FCSTD DOCUMENT  (FreeCAD 0.20R29410 (Git))
Label: wearableV5Plus_m3_May_1_m3_2023
License: All rights reserved
LicenseURL: http://en.wikipedia.org/wiki/All_rights_reserved
objects: Part::Feature×57, Sketcher::SketchObject×23, Part::Extrusion×23, Part::MultiFuse×12, Part::Fillet×10, Part::Cut×10, Part::Box×9, App::Part×9, Part::Cylinder×4, Mesh::Feature×2, Part::Compound×1
note: 149 computed .brp shape members not serialized (recipe doc carries the construction recipe); baked Part::Feature solids carry a one-line shape summary decoded from their .brp

FEATURE [Part::Box] Box  label="batteryPlus"
  AttacherType = Attacher::AttachEngine3D
  Height = 11
  Length = 68
  Placement = pos=(3,3,2) rot=(0,0,1;0rad)
  Width = 56
FEATURE [Mesh::Feature] pisugar3Board
  Placement = pos=(-2.89,36.08,0.25) rot=(-1,0,0;4.71239rad)
FEATURE [Part::Feature] Part__Feature001  label="RaspberryPiZeroW"
  Placement = pos=(36.5,18,19.18) rot=(1,0,0;1.5708rad)
  shape: bbox 65.9 x 31.25 x 4.8 mm, 368 faces, 2 solids (baked)
FEATURE [Part::Feature] Part__Feature  label="ips7100"
  Placement = pos=(-24,0,222) rot=(0.999993,-0.003655,0;3.14159rad)
  shape: bbox 48.14 x 14.05 x 44.14 mm, 1935 faces (baked)
FEATURE [Part::Compound] Compound  label="ips7100s"
  Links = -> [Part__Feature]
  Placement = pos=(13.15,34,29) rot=(0,0.707107,0.707107;3.15032rad)
FEATURE [Part::Feature] Part__Feature002  label="Printed Circuit Board"
  shape: bbox 25.4 x 17.78 x 1.6 mm, 42 faces (baked)
FEATURE [Part::Feature] Part__Feature003  label="EAHC2835WD6"
  shape: bbox 3.513 x 2.813 x 0.7485 mm, 108 faces, 4 solids (baked)
FEATURE [Part::Feature] Part__Feature004  label="AS7341 v2"
  Placement = pos=(0,-0.339822,1.6) rot=(0,0,1;0rad)
  shape: bbox 2 x 3.1 x 1.1 mm, 267 faces, 26 solids (baked)
FEATURE [Part::Feature] Part__Feature005  label="CAPC-0805-T0.95-BN v1"
  Placement = pos=(-5.01759,-3.15294,1.6) rot=(0,0,1;0rad)
  shape: bbox 2.1 x 1.35 x 0.95 mm, 42 faces (baked)
FEATURE [Part::Feature] Part__Feature006  label="CAPC-0805-T0.95-BN v002"
  Placement = pos=(-5.48627,2.66154,1.6) rot=(0,0,-1;1.5708rad)
  shape: bbox 1.35 x 2.1 x 0.95 mm, 42 faces (baked)
FEATURE [Part::Feature] Part__Feature007  label="CAPC-0805-T0.95-BN v003"
  Placement = pos=(-3.43627,2.66154,1.6) rot=(0,0,-1;1.5708rad)
  shape: bbox 1.35 x 2.1 x 0.95 mm, 42 faces (baked)
FEATURE [Part::Feature] Part__Feature008  label="CAPC-0603-T0.9-BN v1"
  Placement = pos=(-1.69987,-3.28475,1.6) rot=(0,0,1;0rad)
  shape: bbox 1.7 x 0.9 x 0.9 mm, 42 faces (baked)
FEATURE [Part::Feature] Part__Feature009  label="BODY_MF06A"
  Placement = pos=(0,0,0.762) rot=(0.57735,-0.57735,-0.57735;2.0944rad)
  shape: bbox 1.601 x 2.921 x 1.016 mm, 42 faces (baked)
FEATURE [Part::Feature] Part__Feature010  label="LEAD_MF06A"
  Placement = pos=(-0.9652,-0.9525,0.1016) rot=(0.57735,-0.57735,-0.57735;2.0944rad)
  shape: bbox 0.6223 x 0.3749 x 0.8636 mm, 14 faces (baked)
FEATURE [Part::Feature] Part__Feature011  label="LEAD_MF06A001"
  Placement = pos=(-0.9652,0,0.1016) rot=(0.57735,-0.57735,-0.57735;2.0944rad)
  shape: bbox 0.6223 x 0.3749 x 0.8636 mm, 14 faces (baked)
FEATURE [Part::Feature] Part__Feature012  label="LEAD_MF06A002"
  Placement = pos=(-0.9652,0.9525,0.1016) rot=(0.57735,-0.57735,-0.57735;2.0944rad)
  shape: bbox 0.6223 x 0.3749 x 0.8636 mm, 14 faces (baked)
FEATURE [Part::Feature] Part__Feature013  label="LEAD_MF06A003"
  Placement = pos=(0.9652,-0.9525,0.1016) rot=(0.57735,0.57735,0.57735;2.0944rad)
  shape: bbox 0.6223 x 0.3749 x 0.8636 mm, 14 faces (baked)
FEATURE [Part::Feature] Part__Feature014  label="LEAD_MF06A004"
  Placement = pos=(0.9652,0,0.1016) rot=(0.57735,0.57735,0.57735;2.0944rad)
  shape: bbox 0.6223 x 0.3749 x 0.8636 mm, 14 faces (baked)
FEATURE [Part::Feature] Part__Feature015  label="LEAD_MF06A005"
  Placement = pos=(0.9652,0.9525,0.1016) rot=(0.57735,0.57735,0.57735;2.0944rad)
  shape: bbox 0.6223 x 0.3749 x 0.8636 mm, 14 faces (baked)
FEATURE [Part::Feature] Part__Feature016  label="SOT363 v2"
  Placement = pos=(4.97054,-0.645171,1.675) rot=(0,0,1;3.14159rad)
  shape: bbox 2.1 x 2 x 1.1 mm, 94 faces, 7 solids (baked)
FEATURE [Part::Feature] Part__Feature017  label="LED 0603 single color v1"
  Placement = pos=(-9.18406,3.72778,1.60762) rot=(0,0,1;1.5708rad)
  shape: bbox 1.961 x 0.7932 x 0.7145 mm, 63 faces, 5 solids (baked)
FEATURE [Part::Feature] Part__Feature018  label="RESC-0603 v1"
  Placement = pos=(4.83432,-3.67461,1.6) rot=(0,0,1;0rad)
  shape: bbox 1.7 x 0.9 x 0.55 mm, 52 faces, 3 solids (baked)
FEATURE [Part::Feature] Part__Feature019  label="RESC-0603 v002"
  Placement = pos=(-7.14949,3.61248,1.6) rot=(0,0,-1;1.5708rad)
  shape: bbox 0.9 x 1.7 x 0.55 mm, 52 faces, 3 solids (baked)
FEATURE [Part::Feature] Part__Feature020  label="YC164_RESPACK v1"
  Placement = pos=(2.99591,1.52916,1.6) rot=(0,0,1;0rad)
  shape: bbox 3.2 x 1.6 x 0.61 mm, 172 faces (baked)
FEATURE [Part::Feature] Part__Feature021  label="qwicc v2"
  Placement = pos=(-10.8364,0.0607456,1.65) rot=(0,0,-1;1.5708rad)
  shape: bbox 4.95 x 6 x 2.96 mm, 229 faces, 7 solids (baked)
FEATURE [Part::Feature] Part__Feature022  label="qwicc v003"
  Placement = pos=(10.8256,0.00556102,1.65) rot=(0,0,1;1.5708rad)
  shape: bbox 4.95 x 6 x 2.96 mm, 229 faces, 7 solids (baked)
FEATURE [Part::Feature] Part__Feature023  label="scd30"
  Placement = pos=(20,68.5,5.75) rot=(1,0,0;1.5708rad)
  shape: bbox 35.11 x 23.02 x 7.027 mm, 2292 faces, 25 solids (baked)
FEATURE [App::Part] sot_23_6_v2  label="sot-23-6 v2"
  Group = -> [Part__Feature009,Part__Feature010,Part__Feature011,Part__Feature012,Part__Feature013,Part__Feature014,Part__Feature015]
  Origin = -> Origin
  Placement = pos=(-4.47945,-0.603742,1.69152) rot=(0,0,1;0rad)
FEATURE [App::Part] Adafruit_AS7341_STEMMA_QT_v2  label="bme280"
  Group = -> [Part__Feature002,Part__Feature003,Part__Feature004,Part__Feature005,Part__Feature006,Part__Feature007,Part__Feature008,sot_23_6_v2,Part__Feature016,Part__Feature017,Part__Feature018,Part__Feature019,Part__Feature020,Part__Feature021,Part__Feature022]
  Origin = -> Origin001
  Placement = pos=(53,69,12) rot=(0,1,0;3.14159rad)
FEATURE [Part::Box] Box002  label="bottom"
  AttacherType = Attacher::AttachEngine3D
  Height = 27
  Length = 74
  Width = 91
FEATURE [Part::Fillet] Fillet  label="bottom002"
  Base = -> Box002
  Edges = 8 edges r=2: [Edge1,Edge3,Edge4,Edge5,Edge7,Edge8,Edge9,Edge11]
FEATURE [Part::Box] Box003  label="bottom001"
  AttacherType = Attacher::AttachEngine3D
  Height = 39
  Length = 70
  Placement = pos=(2,2,2) rot=(0,0,1;0rad)
  Width = 87
FEATURE [Part::Fillet] Fillet001  label="bottomCut"
  Base = -> Box003
  Edges = 8 edges r=2: [Edge1,Edge3,Edge4,Edge5,Edge7,Edge8,Edge9,Edge11]
FEATURE [Part::Cut] Cut  label="bottom003"
  Base = -> Fillet
  Tool = -> Fillet001
FEATURE [Part::Feature] Part__Feature024  label="Board"
  shape: bbox 25.4 x 25.4 x 1.57 mm, 211 faces (baked)
FEATURE [Part::Feature] Part__Feature025  label="QFN24_4MM"
  Placement = pos=(12.1412,14.4526,1.57) rot=(0,0,1;3.92699rad)
  shape: bbox 5.657 x 5.657 x 0.9 mm, 172 faces (baked)
FEATURE [Part::Feature] Part__Feature026  label="Part 5"
  shape: bbox 0.48 x 0.6603 x 0.6 mm, 14 faces (baked)
FEATURE [Part::Feature] Part__Feature027  label="Part 6"
  shape: bbox 0.48 x 0.6603 x 0.6 mm, 14 faces (baked)
FEATURE [Part::Feature] Part__Feature028  label="Part 4"
  shape: bbox 0.48 x 0.6603 x 0.6 mm, 14 faces (baked)
FEATURE [Part::Feature] Part__Feature029  label="Part 3"
  shape: bbox 0.48 x 0.6603 x 0.6 mm, 14 faces (baked)
FEATURE [Part::Feature] Part__Feature030  label="Part 2"
  shape: bbox 0.48 x 0.6603 x 0.6 mm, 14 faces (baked)
FEATURE [Part::Feature] Part__Feature031  label="Part 1"
  shape: bbox 3 x 1.4 x 1 mm, 10 faces (baked)
FEATURE [App::Part] _6700497  label="36700497"
  Group = -> [Part__Feature026,Part__Feature027,Part__Feature028,Part__Feature029,Part__Feature030,Part__Feature031]
  Origin = -> Origin002
  Placement = pos=(0,0,0) rot=(0,0,1;3.14159rad)
FEATURE [App::Part] SOT23_5  label="SOT23-5"
  Group = -> [_6700497]
  Origin = -> Origin003
  Placement = pos=(2.54,6.985,1.57) rot=(0,0,1;3.14159rad)
FEATURE [Part::Feature] Part__Feature032  label="Pin1"
  shape: bbox 0.6224 x 1.252 x 1.252 mm, 37 faces (baked)
FEATURE [Part::Feature] Part__Feature033  label="Pin2"
  shape: bbox 0.6224 x 1.252 x 1.252 mm, 37 faces (baked)
FEATURE [Part::Feature] Part__Feature034  label="CeramicBody"
  shape: bbox 1.8 x 1.23 x 1.23 mm, 10 faces (baked)
FEATURE [App::Part] _603_NO  label="0603-NO"
  Group = -> [Part__Feature032,Part__Feature033,Part__Feature034]
  Origin = -> Origin004
  Placement = pos=(16.51,8.382,1.57) rot=(0,0,1;0rad)
FEATURE [Part::Feature] Part__Feature035  label="0603-NO (1)"
  Placement = pos=(23.241,6.223,1.57) rot=(0,0,1;0rad)
  shape: bbox 1.7 x 0.9 x 0.55 mm, 52 faces, 3 solids (baked)
FEATURE [Part::Feature] Part__Feature036  label="0603-NO (2)"
  Placement = pos=(13.3858,8.4328,1.57) rot=(0,0,1;0rad)
  shape: bbox 1.7 x 0.9 x 0.55 mm, 52 faces, 3 solids (baked)
FEATURE [Part::Feature] Part__Feature037  label="0603-NO (3)"
  Placement = pos=(1.905,18.923,1.57) rot=(0,0,1;3.14159rad)
  shape: bbox 1.7 x 0.9 x 0.55 mm, 52 faces, 3 solids (baked)
FEATURE [Part::Feature] Part__Feature038  label="Pin1 (1)"
  shape: bbox 0.6224 x 1.252 x 1.252 mm, 37 faces (baked)
FEATURE [Part::Feature] Part__Feature039  label="Pin2 (1)"
  shape: bbox 0.6224 x 1.252 x 1.252 mm, 37 faces (baked)
FEATURE [Part::Feature] Part__Feature040  label="CeramicBody (1)"
  shape: bbox 1.8 x 1.23 x 1.23 mm, 10 faces (baked)
FEATURE [App::Part] _805_NO  label="0805-NO"
  Group = -> [Part__Feature038,Part__Feature039,Part__Feature040]
  Origin = -> Origin005
  Placement = pos=(7.874,13.589,1.57) rot=(0,0,1;1.5708rad)
FEATURE [Part::Feature] Part__Feature041  label="Pin1 (2)"
  shape: bbox 0.6224 x 1.252 x 1.252 mm, 37 faces (baked)
FEATURE [Part::Feature] Part__Feature042  label="Pin2 (2)"
  shape: bbox 0.6224 x 1.252 x 1.252 mm, 37 faces (baked)
FEATURE [Part::Feature] Part__Feature043  label="CeramicBody (2)"
  shape: bbox 1.8 x 1.23 x 1.23 mm, 10 faces (baked)
FEATURE [App::Part] _805_NO__1_  label="0805-NO (1)"
  Group = -> [Part__Feature041,Part__Feature042,Part__Feature043]
  Origin = -> Origin006
  Placement = pos=(12.827,6.223,1.57) rot=(0,0,1;3.14159rad)
FEATURE [Part::Feature] Part__Feature044  label="CHIPLED_0603_NOOUTLINE"
  Placement = pos=(23.368,8.509,1.57) rot=(0,0,1;1.5708rad)
  shape: bbox 1.616 x 0.8 x 0.4 mm, 133 faces (baked)
FEATURE [Part::Feature] Part__Feature045  label="CHIPLED_0603_NOOUTLINE (1)"
  Placement = pos=(1.905,16.764,1.57) rot=(0,0,-1;1.5708rad)
  shape: bbox 1.616 x 0.8 x 0.4 mm, 133 faces (baked)
FEATURE [Part::Feature] Part__Feature046  label="JST_SH4"
  Placement = pos=(22.86,12.7,1.57) rot=(0,0,1;1.5708rad)
  shape: bbox 4.95 x 6 x 2.96 mm, 229 faces, 7 solids (baked)
FEATURE [Part::Feature] Part__Feature047  label="JST_SH4 (1)"
  Placement = pos=(2.54,12.7,1.57) rot=(0,0,-1;1.5708rad)
  shape: bbox 4.95 x 6 x 2.96 mm, 229 faces, 7 solids (baked)
FEATURE [Part::Feature] Part__Feature048  label="NEO3535_REVERSE"
  Placement = pos=(12.7,23.114,0) rot=(0,1,0;3.14159rad)
  shape: bbox 5.88 x 2.8 x 1.78 mm, 41 faces, 5 solids (baked)
FEATURE [Part::Feature] Part__Feature049  label="RESPACK_4X0603"
  Placement = pos=(22.86,18.415,1.57) rot=(0,0,1;3.14159rad)
  shape: bbox 3.2 x 1.6 x 0.61 mm, 172 faces (baked)
FEATURE [Part::Feature] Part__Feature050  label="SOT363"
  Placement = pos=(17.399,12.192,1.57) rot=(0,0,-1;1.5708rad)
  shape: bbox 2.208 x 2.208 x 1.121 mm, 178 faces, 4 solids (baked)
FEATURE [App::Part] Packages
  Group = -> [Part__Feature025,SOT23_5,_603_NO,Part__Feature035,Part__Feature036,Part__Feature037,_805_NO,_805_NO__1_,Part__Feature044,Part__Feature045,Part__Feature046,Part__Feature047,Part__Feature048,Part__Feature049,Part__Feature050]
  Origin = -> Origin007
FEATURE [Sketcher::SketchObject] Sketch
  FullyConstrained = true
  sketch-geometry (39):
    g0: LineSegment StartX=3 StartY=43.5 StartZ=0 EndX=3 EndY=34.5 EndZ=0
    g1: LineSegment StartX=3 StartY=34.5 StartZ=0 EndX=70.5 EndY=34.5 EndZ=0
    g2: LineSegment StartX=3 StartY=43.5 StartZ=0 EndX=10.5 EndY=43.5 EndZ=0
    g3: LineSegment StartX=3 StartY=71 StartZ=0 EndX=10.5 EndY=71 EndZ=0
    g4: LineSegment StartX=3 StartY=71 StartZ=0 EndX=3 EndY=80 EndZ=0
    g5: LineSegment StartX=70.5 StartY=80 StartZ=0 EndX=70.5 EndY=71 EndZ=0
    g6: LineSegment StartX=70.5 StartY=71 StartZ=0 EndX=62.5 EndY=71 EndZ=0
    g7: LineSegment StartX=62.5 StartY=71 StartZ=0 EndX=62.5 EndY=43 EndZ=0
    g8: LineSegment StartX=62.5 StartY=43 StartZ=0 EndX=70.5 EndY=43 EndZ=0
    g9: LineSegment StartX=70.5 StartY=43 StartZ=0 EndX=70.5 EndY=34.5 EndZ=0
    g10: GeomPoint X=70.5 Y=34.5 Z=0
    g11: GeomPoint X=70.5 Y=34.5 Z=0
    g12: GeomPoint X=70.5 Y=34.5 Z=0
    g13: GeomPoint X=70.5 Y=34.5 Z=0
    g14: GeomPoint X=70.5 Y=34.5 Z=0
    g15: LineSegment StartX=10.5 StartY=43.5 StartZ=0 EndX=10.5 EndY=71 EndZ=0
    g16: Circle CenterX=7.5 CenterY=75.5 CenterZ=0 NormalX=0 NormalY=0 NormalZ=1 AngleXU=0 Radius=1.6
    g17: Circle CenterX=7.5 CenterY=39 CenterZ=0 NormalX=0 NormalY=0 NormalZ=1 AngleXU=0 Radius=1.6
    g18: Circle CenterX=66.5 CenterY=39 CenterZ=0 NormalX=0 NormalY=0 NormalZ=1 AngleXU=0 Radius=1.6
    g19: Circle CenterX=66.5 CenterY=75.5 CenterZ=0 NormalX=0 NormalY=0 NormalZ=1 AngleXU=0 Radius=1.6
    g20: Circle CenterX=14.2 CenterY=70.46 CenterZ=0 NormalX=0 NormalY=0 NormalZ=1 AngleXU=0 Radius=1.6
    g21: Circle CenterX=38.54 CenterY=77.84 CenterZ=0 NormalX=0 NormalY=0 NormalZ=1 AngleXU=0 Radius=1.6
    g22: Circle CenterX=58.86 CenterY=77.84 CenterZ=0 NormalX=0 NormalY=0 NormalZ=1 AngleXU=0 Radius=1.6
    g23: Circle CenterX=38.54 CenterY=57.52 CenterZ=0 NormalX=0 NormalY=0 NormalZ=1 AngleXU=0 Radius=1.6
    g24: Circle CenterX=58.86 CenterY=57.52 CenterZ=0 NormalX=0 NormalY=0 NormalZ=1 AngleXU=0 Radius=1.6
    g25: Circle CenterX=38.54 CenterY=52.33 CenterZ=0 NormalX=0 NormalY=0 NormalZ=1 AngleXU=0 Radius=1.6
    g26: Circle CenterX=58.86 CenterY=52.33 CenterZ=0 NormalX=0 NormalY=0 NormalZ=1 AngleXU=0 Radius=1.6
    g27: Circle CenterX=38.54 CenterY=39.63 CenterZ=0 NormalX=0 NormalY=0 NormalZ=1 AngleXU=0 Radius=1.6
    g28: Circle CenterX=58.86 CenterY=39.63 CenterZ=0 NormalX=0 NormalY=0 NormalZ=1 AngleXU=0 Radius=1.6
    g29: Circle CenterX=30.43 CenterY=38.46 CenterZ=0 NormalX=0 NormalY=0 NormalZ=1 AngleXU=0 Radius=1.6
    g30: ArcOfCircle CenterX=48.54 CenterY=70.34 CenterZ=0 NormalX=0 NormalY=0 NormalZ=1 AngleXU=0 Radius=5 StartAngle=-9e-16 EndAngle=3.14159
    g31: ArcOfCircle CenterX=48.54 CenterY=42.63 CenterZ=0 NormalX=0 NormalY=0 NormalZ=1 AngleXU=0 Radius=5 StartAngle=3.14159 EndAngle=6.28319
    g32: LineSegment StartX=43.54 StartY=70.34 StartZ=0 EndX=43.54 EndY=42.63 EndZ=0
    g33: LineSegment StartX=53.54 StartY=42.63 StartZ=0 EndX=53.54 EndY=70.34 EndZ=0
    g34: ArcOfCircle CenterX=22.2 CenterY=70.34 CenterZ=0 NormalX=0 NormalY=0 NormalZ=1 AngleXU=0 Radius=5 StartAngle=0 EndAngle=3.14159
    g35: ArcOfCircle CenterX=22.2 CenterY=42.63 CenterZ=0 NormalX=0 NormalY=0 NormalZ=1 AngleXU=0 Radius=5 StartAngle=3.14159 EndAngle=6.28319
    g36: LineSegment StartX=17.2 StartY=70.34 StartZ=0 EndX=17.2 EndY=42.63 EndZ=0
    g37: LineSegment StartX=27.2 StartY=42.63 StartZ=0 EndX=27.2 EndY=70.34 EndZ=0
    g38: LineSegment StartX=3 StartY=80 StartZ=0 EndX=70.5 EndY=80 EndZ=0
  constraints (103):
    c: Vertical(g0)
    c: Coincident(g1,g0)
    c: Horizontal(g1)
    c: Coincident(g2,g0)
    c: Coincident(g4,g3)
    c: Vertical(g4)
    c: Coincident(g6,g5)
    c: Horizontal(g6)
    c: Coincident(g7,g6)
    c: Vertical(g7)
    c: Horizontal(g8)
    c: Horizontal(g2)
    c: Coincident(g10,g9)
    c: Coincident(g11,g1)
    c: Coincident(g12,g9)
    c: Coincident(g13,g1)
    c: Coincident(g14,g9)
    c: Coincident(g9,g1)
    c: Vertical(g9)
    c: Coincident(g15,g2)
    c: Coincident(g15,g3)
    c: Vertical(g15)
    c: Horizontal(g3)
    c: Vertical(g5)
    c: Coincident(g8,g9)
    c: Coincident(g7,g8)
    c: DistanceX(g8,g8) = 8
    c: Radius(g16) = 1.6
    c: DistanceY(g17) = 39
    c: Radius(g17) = 1.6
    c: DistanceX(g18) = 66.5
    c: DistanceY(g17,g18) = 0
    c: Radius(g18) = 1.6
    c: DistanceX(g19,g18) = 0
    c: Radius(g19) = 1.6
    c: DistanceY(g16) = 75.5
    c: DistanceY(g16,g19) = 0
    c: DistanceY(g3,g5) = 0
    c: Radius(g21) = 1.6
    c: DistanceY(g21,g22) = 0
    c: Radius(g22) = 1.6
    c: DistanceX(g21,g22) = 20.32
    c: DistanceX(g23,g21) = 0
    c: Radius(g23) = 1.6
    c: DistanceY(g23,g21) = 20.32
    c: DistanceY(g24,g23) = 0
    c: DistanceX(g24,g22) = 0
    c: Radius(g24) = 1.6
    c: DistanceX(g25,g23) = 0
    c: Radius(g25) = 1.6
    c: DistanceY(g25,g26) = 0
    c: DistanceX(g24,g26) = 0
    c: Radius(g26) = 1.6
    c: DistanceX(g25,g27) = 0
    c: DistanceX(g28,g26) = 0
    c: DistanceY(g27,g25) = 12.7
    c: DistanceY(g28,g27) = 0
    c: Radius(g28) = 1.6
    c: Radius(g27) = 1.6
    c: Radius(g29) = 1.6
    c: DistanceY(g29,g20) = 32
    c: Radius(g20) = 1.6
    c: Tangent(g30,g32) = -1.5708
    c: Tangent(g32,g31) = -1.5708
    c: Tangent(g31,g33) = -1.5708
    c: Tangent(g33,g30) = -1.5708
    c: Equal(g30,g31)
    c: Vertical(g32)
    c: DistanceY(g27,g31) = 3
    c: Radius(g30) = 5
    c: Tangent(g34,g36) = -1.5708
    c: Tangent(g36,g35) = -1.5708
    c: Tangent(g35,g37) = -1.5708
    c: Tangent(g37,g34) = -1.5708
    c: Equal(g34,g35)
    c: Vertical(g36)
    c: Radius(g34) = 5
    c: DistanceY(g34,g30) = 0
    c: DistanceY(g31,g35) = 0
    c: DistanceX(g16,g17) = 0
    c: DistanceX(g0,g3) = 0
    c: Coincident(g38,g4)
    c: Coincident(g38,g5)
    c: Horizontal(g38)
    c: DistanceX(g29) = 30.43
    c: DistanceX(g20) = 14.2
    c: DistanceY(g20) = 70.46
    c: DistanceX(g27) = 38.54
    c: DistanceY(g27) = 39.63
    c: DistanceY(g23) = 57.52
    c: DistanceY(g3,g16) = 4.5
    c: DistanceY(g16,g4) = 4.5
    c: DistanceY(g0,g17) = 4.5
    c: DistanceX(g0,g17) = 4.5
    c: DistanceX(g17) = 7.5
    c: DistanceY(g17,g0) = 4.5
    c: DistanceX(g16,g3) = 3
    c: DistanceX(g19,g5) = 4
    c: DistanceX(g6,g19) = 4
    c: DistanceY(g18,g8) = 4
    c: DistanceX(g25,g31) = 10
    c: DistanceY(g30,g21) = 7.5
    c: DistanceX(g20,g34) = 8
FEATURE [Part::Extrusion] Extrude  label="sensorHold"
  Base = -> Sketch
  Dir = (0,0,1)
  DirMode = 2
  FaceMakerClass = Part::FaceMakerBullseye
  LengthFwd = 4
  LengthRev = 0
  Placement = pos=(0,0,16) rot=(0,0,1;0rad)
  Solid = true
  Symmetric = false
FEATURE [Part::Fillet] Fillet002  label="sensorHold001"
  Base = -> Extrude
  Edges = 12 edges r=3: [Edge1,Edge2,Edge5,Edge8,Edge11,Edge14,Edge17,Edge20,Edge23,Edge26,Edge29,Edge32]
FEATURE [App::Part] Adafruit_I2C_QT_Rotary_Encoder_v2  label="gps"
  Group = -> [Part__Feature024,Packages,Sketch,Extrude,Fillet002]
  Origin = -> Origin008
  Placement = pos=(45,79,28.25) rot=(-1,0,0;1.5708rad)
FEATURE [Sketcher::SketchObject] Sketch001
  FullyConstrained = true
  sketch-geometry (10):
    g0: LineSegment StartX=19.03 StartY=74.44 StartZ=0 EndX=19.03 EndY=77.44 EndZ=0
    g1: LineSegment StartX=16.53 StartY=71.94 StartZ=0 EndX=13.53 EndY=71.94 EndZ=0
    g2: LineSegment StartX=13.53 StartY=71.94 StartZ=0 EndX=13.53 EndY=77.44 EndZ=0
    g3: LineSegment StartX=19.03 StartY=77.44 StartZ=0 EndX=13.53 EndY=77.44 EndZ=0
    g4: ArcOfCircle CenterX=16.53 CenterY=74.44 CenterZ=0 NormalX=0 NormalY=0 NormalZ=1 AngleXU=0 Radius=2.5 StartAngle=4.71239 EndAngle=6.28319
    g5: LineSegment StartX=60.53 StartY=34.86 StartZ=0 EndX=55.03 EndY=34.86 EndZ=0
    g6: LineSegment StartX=55.03 StartY=34.86 StartZ=0 EndX=55.03 EndY=37.86 EndZ=0
    g7: LineSegment StartX=60.53 StartY=34.86 StartZ=0 EndX=60.53 EndY=40.36 EndZ=0
    g8: LineSegment StartX=60.53 StartY=40.36 StartZ=0 EndX=57.53 EndY=40.36 EndZ=0
    g9: ArcOfCircle CenterX=57.53 CenterY=37.86 CenterZ=0 NormalX=0 NormalY=0 NormalZ=1 AngleXU=0 Radius=2.5 StartAngle=1.5708 EndAngle=3.14159
  constraints (32):
    c: Vertical(g0)
    c: Horizontal(g1)
    c: Vertical(g2)
    c: Coincident(g2,g3)
    c: Coincident(g0,g3)
    c: Horizontal(g3)
    c: DistanceX(g3,g3) = 5.5
    c: DistanceY(g2,g2) = 5.5
    c: DistanceY(g4,g4) = 0
    c: DistanceX(g4,g4) = 0
    c: Coincident(g1,g4)
    c: Coincident(g0,g4)
    c: Radius(g4) = 2.5
    c: DistanceX(g4) = 16.53
    c: DistanceY(g4) = 74.44
    c: Coincident(g1,g2)
    c: Horizontal(g5)
    c: Vertical(g6)
    c: Vertical(g7)
    c: Horizontal(g8)
    c: Coincident(g7,g8)
    c: Coincident(g8,g9)
    c: Coincident(g6,g9)
    c: Coincident(g5,g6)
    c: Coincident(g5,g7)
    c: DistanceX(g5,g5) = 5.5
    c: DistanceY(g7,g7) = 5.5
    c: DistanceY(g6,g6) = 3
    c: DistanceX(g8,g8) = 3
    c: Radius(g9) = 2.5
    c: DistanceY(g9,g4) = 36.58
    c: DistanceX(g4,g9) = 41
FEATURE [Part::Extrusion] Extrude001
  Base = -> Sketch001
  Dir = (0,0,1)
  DirMode = 2
  FaceMakerClass = Part::FaceMakerBullseye
  LengthFwd = 4
  LengthRev = 0
  Placement = pos=(0,0,2) rot=(0,0,1;0rad)
  Solid = true
  Symmetric = false
FEATURE [Part::Fillet] Fillet003  label="ipsHoldBottomInDone"
  Base = -> Extrude001
  Edges = 14 edges r=0.5: [Edge4,Edge7,Edge10,Edge11,Edge13,Edge15,Edge19,Edge20,Edge22,Edge23,Edge25,Edge26,Edge28,Edge30]
  Placement = pos=(0,0,13) rot=(0,0,1;0rad)
FEATURE [Sketcher::SketchObject] Sketch002
  FullyConstrained = true
  MapMode = 2
  Support = -> [Cut]
  sketch-geometry (10):
    g0: LineSegment StartX=63 StartY=9.25 StartZ=0 EndX=72 EndY=9.25 EndZ=0
    g1: LineSegment StartX=72 StartY=9.25 StartZ=0 EndX=72 EndY=2 EndZ=0
    g2: LineSegment StartX=72 StartY=2 StartZ=0 EndX=63 EndY=2 EndZ=0
    g3: LineSegment StartX=63 StartY=2 StartZ=0 EndX=63 EndY=9.25 EndZ=0
    g4: LineSegment StartX=2 StartY=9.25 StartZ=0 EndX=10 EndY=9.25 EndZ=0
    g5: LineSegment StartX=10 StartY=9.25 StartZ=0 EndX=10 EndY=2 EndZ=0
    g6: LineSegment StartX=10 StartY=2 StartZ=0 EndX=2 EndY=2 EndZ=0
    g7: LineSegment StartX=2 StartY=2 StartZ=0 EndX=2 EndY=9.25 EndZ=0
    g8: Circle CenterX=7.47 CenterY=6.47 CenterZ=0 NormalX=0 NormalY=0 NormalZ=1 AngleXU=0 Radius=1.35
    g9: Circle CenterX=65.52 CenterY=6.47 CenterZ=0 NormalX=0 NormalY=0 NormalZ=1 AngleXU=0 Radius=1.35
  constraints (30):
    c: Coincident(g0,g1)
    c: Coincident(g1,g2)
    c: Coincident(g2,g3)
    c: Coincident(g3,g0)
    c: Horizontal(g0)
    c: Horizontal(g2)
    c: Vertical(g1)
    c: Vertical(g3)
    c: Coincident(g4,g5)
    c: Coincident(g5,g6)
    c: Coincident(g6,g7)
    c: Coincident(g7,g4)
    c: Horizontal(g4)
    c: Horizontal(g6)
    c: Vertical(g5)
    c: Vertical(g7)
    c: DistanceX(g6) = 2
    c: DistanceY(g6) = 2
    c: DistanceX(g6,g6) = 8
    c: DistanceY(g7,g7) = 7.25
    c: DistanceX(g-1,g1) = 72
    c: DistanceY(g2,g5) = 0
    c: DistanceY(g0,g4) = 0
    c: DistanceX(g2,g2) = 9
    c: DistanceX(g8) = 7.47
    c: Radius(g8) = 1.35
    c: DistanceX(g9) = 65.52
    c: DistanceY(g8,g9) = 0
    c: Radius(g9) = 1.35
    c: DistanceY(g8) = 6.47
FEATURE [Part::Extrusion] Extrude002  label="RaberryPiHold"
  Base = -> Sketch002
  Dir = (0,0,1)
  DirMode = 2
  FaceMakerClass = Part::FaceMakerBullseye
  LengthFwd = 2
  LengthRev = 0
  Placement = pos=(0,0,20.7) rot=(0,0,1;0rad)
  Solid = true
  Symmetric = false
FEATURE [Part::Fillet] Fillet004  label="piHoldBottomInDone"
  Base = -> Extrude002
  Edges = 6 edges: [Edge1 r=2,Edge4 r=1,Edge12 r=1,Edge17 r=2,Edge19 r=1,Edge22 r=1]
FEATURE [Part::Box] Box004  label="top"
  AttacherType = Attacher::AttachEngine3D
  Height = 5
  Length = 74
  Placement = pos=(0,0,27) rot=(0,0,1;0rad)
  Width = 91
FEATURE [Part::Fillet] Fillet005  label="top001"
  Base = -> Box004
  Edges = 8 edges r=1.95: [Edge1,Edge2,Edge3,Edge5,Edge6,Edge7,Edge10,Edge12]
  Placement = pos=(0,0,2) rot=(0,0,1;0rad)
FEATURE [Part::Feature] Part__Feature060  label="logoTopCut"
  Placement = pos=(5.75,8,35) rot=(-1,0,0;1.5708rad)
  shape: bbox 22.79 x 17.08 x 8 mm, 886 faces (baked)
FEATURE [Sketcher::SketchObject] Sketch004
  FullyConstrained = true
  Placement = pos=(0,0,0) rot=(1,0,0;1.5708rad)
  sketch-geometry (46):
    g0: LineSegment StartX=11.75 StartY=19.5 StartZ=0 EndX=21.5 EndY=19.5 EndZ=0
    g1: LineSegment StartX=21.5 StartY=19.5 StartZ=0 EndX=23.75 EndY=22 EndZ=0
    g2: LineSegment StartX=23.75 StartY=22 StartZ=0 EndX=23.75 EndY=25 EndZ=0
    g3: LineSegment StartX=23.75 StartY=25 StartZ=0 EndX=9.5 EndY=25 EndZ=0
    g4: LineSegment StartX=9.5 StartY=25 StartZ=0 EndX=9.5 EndY=22 EndZ=0
    g5: LineSegment StartX=40 StartY=24.5 StartZ=0 EndX=40 EndY=22 EndZ=0
    g6: LineSegment StartX=40 StartY=22 StartZ=0 EndX=42.5 EndY=19.5 EndZ=0
    g7: LineSegment StartX=42.5 StartY=19.5 StartZ=0 EndX=48.7 EndY=19.5 EndZ=0
    g8: LineSegment StartX=48.7 StartY=19.5 StartZ=0 EndX=51.2 EndY=22 EndZ=0
    g9: LineSegment StartX=51.2 StartY=22 StartZ=0 EndX=51.2 EndY=24.5 EndZ=0
    g10: LineSegment StartX=51.2 StartY=24.5 StartZ=0 EndX=40 EndY=24.5 EndZ=0
    g11: LineSegment StartX=52.45 StartY=24.5 StartZ=0 EndX=52.45 EndY=22 EndZ=0
    g12: LineSegment StartX=52.45 StartY=22 StartZ=0 EndX=54.95 EndY=19.5 EndZ=0
    g13: LineSegment StartX=54.95 StartY=19.5 StartZ=0 EndX=61.15 EndY=19.5 EndZ=0
    g14: LineSegment StartX=61.15 StartY=19.5 StartZ=0 EndX=63.65 EndY=22 EndZ=0
    g15: LineSegment StartX=63.65 StartY=22 StartZ=0 EndX=63.65 EndY=24.5 EndZ=0
    g16: LineSegment StartX=63.65 StartY=24.5 StartZ=0 EndX=52.45 EndY=24.5 EndZ=0
    g17: LineSegment StartX=9.5 StartY=22 StartZ=0 EndX=11.75 EndY=19.5 EndZ=0
    g18: ArcOfCircle CenterX=12.3 CenterY=15.45 CenterZ=0 NormalX=0 NormalY=0 NormalZ=1 AngleXU=0 Radius=1 StartAngle=1.5708 EndAngle=3.14159
    g19: LineSegment StartX=11.3 StartY=15.45 StartZ=0 EndX=11.3 EndY=14.2 EndZ=0
    g20: LineSegment StartX=12.3 StartY=16.45 StartZ=0 EndX=16.8 EndY=16.45 EndZ=0
    g21: ArcOfCircle CenterX=16.8 CenterY=15.45 CenterZ=0 NormalX=0 NormalY=0 NormalZ=1 AngleXU=0 Radius=1 StartAngle=3e-16 EndAngle=1.5708
    g22: ArcOfCircle CenterX=16.8 CenterY=14.2 CenterZ=0 NormalX=0 NormalY=0 NormalZ=1 AngleXU=0 Radius=1 StartAngle=4.71239 EndAngle=6.28319
    g23: ArcOfCircle CenterX=12.3 CenterY=14.2 CenterZ=0 NormalX=0 NormalY=0 NormalZ=1 AngleXU=0 Radius=1 StartAngle=3.14159 EndAngle=4.71239
    g24: LineSegment StartX=12.3 StartY=13.2 StartZ=0 EndX=16.8 EndY=13.2 EndZ=0
    g25: LineSegment StartX=17.8 StartY=15.45 StartZ=0 EndX=17.8 EndY=14.2 EndZ=0
    g26: Circle CenterX=18.9 CenterY=16.475 CenterZ=0 NormalX=0 NormalY=0 NormalZ=1 AngleXU=0 Radius=0.5
    g27: Circle CenterX=21.09 CenterY=16.475 CenterZ=0 NormalX=0 NormalY=0 NormalZ=1 AngleXU=0 Radius=0.5
    g28: Circle CenterX=23.28 CenterY=16.475 CenterZ=0 NormalX=0 NormalY=0 NormalZ=1 AngleXU=0 Radius=0.5
    g29: Circle CenterX=25.47 CenterY=16.475 CenterZ=0 NormalX=0 NormalY=0 NormalZ=1 AngleXU=0 Radius=0.5
    g30: LineSegment StartX=44.8 StartY=16.45 StartZ=0 EndX=49.3 EndY=16.45 EndZ=0
    g31: LineSegment StartX=50.3 StartY=15.45 StartZ=0 EndX=50.3 EndY=14.2 EndZ=0
    g32: LineSegment StartX=49.3 StartY=13.2 StartZ=0 EndX=44.8 EndY=13.2 EndZ=0
    g33: LineSegment StartX=43.8 StartY=15.45 StartZ=0 EndX=43.8 EndY=14.2 EndZ=0
    g34: ArcOfCircle CenterX=44.8 CenterY=15.45 CenterZ=0 NormalX=0 NormalY=0 NormalZ=1 AngleXU=0 Radius=1 StartAngle=1.5708 EndAngle=3.14159
    g35: ArcOfCircle CenterX=49.3 CenterY=15.45 CenterZ=0 NormalX=0 NormalY=0 NormalZ=1 AngleXU=0 Radius=1 StartAngle=3e-16 EndAngle=1.5708
    g36: ArcOfCircle CenterX=49.3 CenterY=14.2 CenterZ=0 NormalX=0 NormalY=0 NormalZ=1 AngleXU=0 Radius=1 StartAngle=4.71239 EndAngle=6.28319
    g37: ArcOfCircle CenterX=44.8 CenterY=14.2 CenterZ=0 NormalX=0 NormalY=0 NormalZ=1 AngleXU=0 Radius=1 StartAngle=3.14159 EndAngle=4.71239
    g38: LineSegment StartX=52.25 StartY=15.58 StartZ=0 EndX=52.25 EndY=14.58 EndZ=0
    g39: LineSegment StartX=53.5 StartY=16.83 StartZ=0 EndX=60.5 EndY=16.83 EndZ=0
    g40: LineSegment StartX=53.5 StartY=13.33 StartZ=0 EndX=60.5 EndY=13.33 EndZ=0
    g41: LineSegment StartX=61.75 StartY=15.58 StartZ=0 EndX=61.75 EndY=14.58 EndZ=0
    g42: ArcOfCircle CenterX=53.5 CenterY=15.58 CenterZ=0 NormalX=0 NormalY=0 NormalZ=1 AngleXU=0 Radius=1.25 StartAngle=1.5708 EndAngle=3.14159
    g43: ArcOfCircle CenterX=60.5 CenterY=15.58 CenterZ=0 NormalX=0 NormalY=0 NormalZ=1 AngleXU=0 Radius=1.25 StartAngle=2e-16 EndAngle=1.5708
    g44: ArcOfCircle CenterX=60.5 CenterY=14.58 CenterZ=0 NormalX=0 NormalY=0 NormalZ=1 AngleXU=0 Radius=1.25 StartAngle=4.7124 EndAngle=6.28319
    g45: ArcOfCircle CenterX=53.5 CenterY=14.58 CenterZ=0 NormalX=0 NormalY=0 NormalZ=1 AngleXU=0 Radius=1.25 StartAngle=3.14159 EndAngle=4.71239
  constraints (150):
    c: Horizontal(g0)
    c: Coincident(g0,g1)
    c: Coincident(g1,g2)
    c: Coincident(g2,g3)
    c: Horizontal(g3)
    c: Coincident(g3,g4)
    c: Vertical(g4)
    c: Coincident(g5,g6)
    c: Coincident(g6,g7)
    c: Horizontal(g7)
    c: Coincident(g7,g8)
    c: Coincident(g8,g9)
    c: Vertical(g9)
    c: Coincident(g9,g10)
    c: Coincident(g10,g5)
    c: Coincident(g11,g12)
    c: Coincident(g12,g13)
    c: Horizontal(g13)
    c: Coincident(g13,g14)
    c: Coincident(g14,g15)
    c: Vertical(g15)
    c: Coincident(g15,g16)
    c: Coincident(g16,g11)
    c: Horizontal(g16)
    c: Coincident(g17,g4)
    c: Coincident(g0,g17)
    c: DistanceX(g3) = 9.5
    c: DistanceX(g3,g3) = 14.25
    c: Vertical(g2)
    c: DistanceY(g3) = 25
    c: DistanceY(g4) = 22
    c: DistanceY(g4,g1) = 0
    c: DistanceX(g4,g0) = 2.25
    c: DistanceX(g0,g1) = 2.25
    c: Horizontal(g10)
    c: Vertical(g5)
    c: Vertical(g11)
    c: DistanceX(g5) = 40
    c: DistanceX(g5,g9) = 11.2
    c: DistanceY(g11,g9) = 0
    c: DistanceY(g5,g5) = 2.5
    c: DistanceY(g8,g5) = 0
    c: DistanceY(g11,g8) = 0
    c: DistanceY(g14,g11) = 0
    c: DistanceY(g6,g5) = 2.5
    c: DistanceX(g5,g6) = 2.5
    c: DistanceX(g7,g8) = 2.5
    c: DistanceX(g9,g11) = 1.25
    c: DistanceY(g12,g7) = 0
    c: DistanceX(g11,g12) = 2.5
    c: DistanceX(g13,g14) = 2.5
    c: DistanceX(g11,g15) = 11.2
    c: DistanceY(g0,g4) = 2.5
    c: DistanceY(g5) = 24.5
    c: Coincident(g19,g18)
    c: Vertical(g19)
    c: Horizontal(g20)
    c: Coincident(g21,g20)
    c: Coincident(g23,g19)
    c: Coincident(g24,g23)
    c: Coincident(g24,g22)
    c: Horizontal(g24)
    c: Coincident(g25,g21)
    c: Coincident(g25,g22)
    c: Vertical(g25)
    c: Coincident(g18,g20)
    c: Radius(g18) = 1
    c: Angle(g18) = 1.5708
    c: Angle(g21) = 1.5708
    c: Angle(g22) = 1.5708
    c: Angle(g23) = 1.5708
    c: DistanceX(g23) = 12.3
    c: DistanceY(g23) = 13.2
    c: DistanceX(g19) = 11.3
    c: DistanceY(g23,g19) = 0
    c: DistanceY(g18,g18) = 0
    c: DistanceX(g21,g20) = 0
    c: Radius(g21) = 1
    c: Radius(g22) = 1
    c: DistanceX(g22,g22) = 0
    c: DistanceX(g18,g20) = 4.5
    c: DistanceX(g26) = 18.9
    c: Radius(g26) = 0.5
    c: DistanceY(g26) = 16.475
    c: DistanceX(g26,g27) = 2.19
    c: DistanceY(g26,g27) = 0
    c: DistanceY(g28,g27) = 0
    c: DistanceY(g29,g28) = 0
    c: DistanceX(g27,g28) = 2.19
    c: Radius(g27) = 0.5
    c: Radius(g28) = 0.5
    c: Radius(g29) = 0.5
    c: DistanceX(g28,g29) = 2.19
    c: DistanceY(g23,g18) = 1.25
    c: Horizontal(g30)
    c: Vertical(g31)
    c: Vertical(g33)
    c: Coincident(g33,g34)
    c: Coincident(g33,g37)
    c: Coincident(g32,g37)
    c: Coincident(g32,g36)
    c: Coincident(g31,g36)
    c: Coincident(g31,g35)
    c: Coincident(g30,g35)
    c: Coincident(g30,g34)
    c: Angle(g34) = 1.5708
    c: Angle(g35) = 1.5708
    c: Angle(g37) = 1.5708
    c: Angle(g36) = 1.5708
    c: DistanceY(g18,g34) = 0
    c: DistanceY(g34,g33) = 0
    c: Radius(g34) = 1
    c: DistanceY(g33,g37) = 0
    c: Radius(g37) = 1
    c: Radius(g36) = 1
    c: Radius(g35) = 1
    c: DistanceY(g33,g23) = 0
    c: DistanceY(g31,g36) = 0
    c: Horizontal(g32)
    c: DistanceX(g35,g30) = 0
    c: DistanceX(g32,g32) = 4.5
    c: Vertical(g38)
    c: Horizontal(g39)
    c: Horizontal(g40)
    c: Vertical(g41)
    c: Coincident(g42,g38)
    c: Coincident(g42,g39)
    c: Coincident(g43,g39)
    c: Coincident(g45,g38)
    c: Coincident(g45,g40)
    c: Coincident(g40,g44)
    c: Coincident(g41,g44)
    c: Coincident(g41,g43)
    c: DistanceX(g42) = 53.5
    c: DistanceY(g42) = 15.58
    c: DistanceX(g42,g45) = 0
    c: DistanceY(g45,g42) = 1
    c: Radius(g42) = 1.25
    c: Radius(g44) = 1.25
    c: Radius(g43) = 1.25
    c: DistanceX(g45,g40) = 0
    c: DistanceX(g42,g39) = 0
    c: DistanceY(g42,g43) = 0
    c: DistanceY(g44,g45) = 0
    c: DistanceY(g45,g38) = 0
    c: DistanceX(g42,g43) = 7
    c: DistanceX(g18,g34) = 32.5
    c: DistanceY(g41,g44) = 0
    c: DistanceY(g43,g41) = 0
    c: Angle(g42) = 1.5708
FEATURE [Part::Extrusion] Extrude004  label="lightBottomCutDone"
  Base = -> Sketch004
  Dir = (0,-1,2e-16)
  DirMode = 2
  FaceMakerClass = Part::FaceMakerBullseye
  LengthFwd = 2
  LengthRev = 0
  Placement = pos=(0,2,0) rot=(0,0,1;0rad)
  Solid = true
  Symmetric = false
FEATURE [Sketcher::SketchObject] Sketch007
  FullyConstrained = true
  sketch-geometry (32):
    g0: LineSegment StartX=4 StartY=85 StartZ=0 EndX=6 EndY=85 EndZ=0
    g1: LineSegment StartX=6 StartY=85 StartZ=0 EndX=-3.99999 EndY=67.6795 EndZ=0
    g2: LineSegment StartX=-3.99999 StartY=67.6795 StartZ=0 EndX=-5.99999 EndY=67.6795 EndZ=0
    g3: LineSegment StartX=-5.99999 StartY=67.6795 StartZ=0 EndX=4 EndY=85 EndZ=0
    g4: LineSegment StartX=-5.99999 StartY=60.6795 StartZ=0 EndX=-3.99999 EndY=60.6795 EndZ=0
    g5: LineSegment StartX=-5.99999 StartY=60.6795 StartZ=0 EndX=4 EndY=78 EndZ=0
    g6: LineSegment StartX=4 StartY=78 StartZ=0 EndX=6 EndY=78 EndZ=0
    g7: LineSegment StartX=6 StartY=78 StartZ=0 EndX=-3.99999 EndY=60.6795 EndZ=0
    g8: LineSegment StartX=-3.99999 StartY=53.6795 StartZ=0 EndX=-5.99999 EndY=53.6795 EndZ=0
    g9: LineSegment StartX=-5.99999 StartY=53.6795 StartZ=0 EndX=4 EndY=71 EndZ=0
    g10: LineSegment StartX=4 StartY=71 StartZ=0 EndX=6 EndY=71 EndZ=0
    g11: LineSegment StartX=6 StartY=71 StartZ=0 EndX=-3.99999 EndY=53.6795 EndZ=0
    g12: LineSegment StartX=4 StartY=64 StartZ=0 EndX=6 EndY=64 EndZ=0
    g13: LineSegment StartX=6 StartY=64 StartZ=0 EndX=-3.99999 EndY=46.6795 EndZ=0
    g14: LineSegment StartX=-3.99999 StartY=46.6795 StartZ=0 EndX=-5.99999 EndY=46.6795 EndZ=0
    g15: LineSegment StartX=-5.99999 StartY=46.6795 StartZ=0 EndX=4 EndY=64 EndZ=0
    g16: LineSegment StartX=70 StartY=85 StartZ=0 EndX=68 EndY=85 EndZ=0
    g17: LineSegment StartX=68 StartY=85 StartZ=0 EndX=78 EndY=67.6795 EndZ=0
    g18: LineSegment StartX=78 StartY=67.6795 StartZ=0 EndX=80 EndY=67.6795 EndZ=0
    g19: LineSegment StartX=80 StartY=67.6795 StartZ=0 EndX=70 EndY=85 EndZ=0
    g20: LineSegment StartX=68 StartY=78 StartZ=0 EndX=70 EndY=78 EndZ=0
    g21: LineSegment StartX=70 StartY=78 StartZ=0 EndX=80 EndY=60.6795 EndZ=0
    g22: LineSegment StartX=80 StartY=60.6795 StartZ=0 EndX=78 EndY=60.6795 EndZ=0
    g23: LineSegment StartX=78 StartY=60.6795 StartZ=0 EndX=68 EndY=78 EndZ=0
    g24: LineSegment StartX=68 StartY=71 StartZ=0 EndX=70 EndY=71 EndZ=0
    g25: LineSegment StartX=70 StartY=71 StartZ=0 EndX=80 EndY=53.6795 EndZ=0
    g26: LineSegment StartX=80 StartY=53.6795 StartZ=0 EndX=78 EndY=53.6795 EndZ=0
    g27: LineSegment StartX=78 StartY=53.6795 StartZ=0 EndX=68 EndY=71 EndZ=0
    g28: LineSegment StartX=68 StartY=64 StartZ=0 EndX=70 EndY=64 EndZ=0
    g29: LineSegment StartX=70 StartY=64 StartZ=0 EndX=80 EndY=46.6795 EndZ=0
    g30: LineSegment StartX=80 StartY=46.6795 StartZ=0 EndX=78 EndY=46.6795 EndZ=0
    g31: LineSegment StartX=78 StartY=46.6795 StartZ=0 EndX=68 EndY=64 EndZ=0
  constraints (96):
    c: Coincident(g3,g0)
    c: DistanceX(g2,g2) = 2
    c: DistanceX(g0,g0) = 2
    c: Angle(g1) = -2.0944
    c: Distance(g3) = 20
    c: Coincident(g2,g3)
    c: DistanceX(g0) = 4
    c: DistanceY(g0) = 85
    c: Coincident(g4,g5)
    c: Coincident(g6,g7)
    c: Coincident(g7,g4)
    c: Horizontal(g6)
    c: DistanceX(g5,g0) = 0
    c: DistanceY(g5,g0) = 7
    c: DistanceX(g2,g4) = 0
    c: DistanceX(g1,g4) = 0
    c: DistanceY(g4,g2) = 7
    c: Horizontal(g4)
    c: Angle(g5) = 1.0472
    c: Horizontal(g8)
    c: Coincident(g9,g8)
    c: Horizontal(g10)
    c: Coincident(g11,g8)
    c: Coincident(g9,g10)
    c: Coincident(g10,g11)
    c: DistanceX(g5,g9) = 0
    c: DistanceX(g10,g6) = 0
    c: DistanceY(g9,g5) = 7
    c: DistanceY(g8,g4) = 7
    c: DistanceX(g8,g4) = 0
    c: DistanceX(g4,g8) = 0
    c: Horizontal(g12)
    c: Coincident(g13,g12)
    c: Horizontal(g14)
    c: Coincident(g15,g12)
    c: Coincident(g1,g2)
    c: Horizontal(g2)
    c: DistanceX(g12,g12) = 2
    c: DistanceX(g9,g12) = 0
    c: DistanceY(g12,g9) = 7
    c: DistanceY(g14,g8) = 7
    c: Coincident(g14,g13)
    c: Coincident(g14,g15)
    c: DistanceX(g14,g8) = 0
    c: DistanceX(g8,g13) = 0
    c: Horizontal(g16)
    c: Coincident(g17,g16)
    c: Coincident(g18,g17)
    c: Horizontal(g18)
    c: Coincident(g19,g16)
    c: DistanceX(g16,g16) = 2
    c: DistanceX(g0,g16) = 66
    c: DistanceY(g16,g0) = 0
    c: Distance(g17) = 20
    c: Coincident(g18,g19)
    c: Angle(g19) = 2.0944
    c: DistanceX(g18,g18) = 2
    c: Horizontal(g20)
    c: Coincident(g21,g20)
    c: Coincident(g22,g21)
    c: Coincident(g23,g20)
    c: Coincident(g25,g24)
    c: Coincident(g26,g25)
    c: Coincident(g27,g24)
    c: Coincident(g29,g28)
    c: Coincident(g30,g29)
    c: Coincident(g31,g28)
    c: DistanceY(g20,g6) = 0
    c: DistanceY(g24,g9) = 0
    c: DistanceY(g28,g12) = 0
    c: DistanceX(g16,g20) = 0
    c: DistanceX(g24,g20) = 0
    c: DistanceX(g28,g24) = 0
    c: Horizontal(g28)
    c: Horizontal(g24)
    c: DistanceX(g24,g24) = 2
    c: DistanceX(g28,g28) = 2
    c: Horizontal(g22)
    c: Horizontal(g26)
    c: Horizontal(g30)
    c: Coincident(g26,g27)
    c: Coincident(g22,g23)
    c: DistanceX(g17,g22) = 0
    c: DistanceX(g22,g26) = 0
    c: DistanceX(g26,g26) = 2
    c: DistanceX(g22,g22) = 2
    c: Coincident(g30,g31)
    c: DistanceX(g30,g30) = 2
    c: DistanceX(g26,g30) = 0
    c: DistanceY(g30,g26) = 7
    c: DistanceY(g26,g22) = 7
    c: DistanceY(g22,g17) = 7
    c: DistanceX(g20,g20) = 2
    c: Coincident(g0,g1)
    c: DistanceX(g6,g6) = 2
    c: Coincident(g5,g6)
FEATURE [Part::Extrusion] Extrude007  label="ventsBottomCut"
  Base = -> Sketch007
  Dir = (0,0,1)
  DirMode = 2
  FaceMakerClass = Part::FaceMakerBullseye
  LengthFwd = 19
  LengthRev = 0
  Placement = pos=(0,0,4) rot=(0,0,1;0rad)
  Solid = true
  Symmetric = false
FEATURE [Sketcher::SketchObject] Sketch009
  FullyConstrained = true
  MapMode = 4
  Placement = pos=(0,0,0) rot=(0.57735,0.57735,0.57735;2.0944rad)
  sketch-geometry (1):
    g0: Circle CenterX=79 CenterY=2 CenterZ=0 NormalX=0 NormalY=0 NormalZ=1 AngleXU=0 Radius=2
  constraints (3):
    c: DistanceX(g0) = 79
    c: DistanceY(g0) = 2
    c: Radius(g0) = 2
FEATURE [Part::Extrusion] Extrude009  label="bottomInTagHoldInDone"
  Base = -> Sketch009
  Dir = (1,0,0)
  DirMode = 2
  FaceMakerClass = Part::FaceMakerBullseye
  LengthFwd = 70
  LengthRev = 0
  Placement = pos=(2,10,0) rot=(0,0,1;0rad)
  Solid = true
  Symmetric = false
FEATURE [Sketcher::SketchObject] Sketch011
  FullyConstrained = true
  Placement = pos=(0,0,0) rot=(0.57735,0.57735,0.57735;2.0944rad)
  sketch-geometry (2):
    g0: Circle CenterX=79 CenterY=2 CenterZ=0 NormalX=0 NormalY=0 NormalZ=1 AngleXU=0 Radius=3.5
    g1: Circle CenterX=79 CenterY=2 CenterZ=0 NormalX=0 NormalY=0 NormalZ=1 AngleXU=0 Radius=2
  constraints (5):
    c: Radius(g0) = 3.5
    c: Radius(g1) = 2
    c: Coincident(g0,g1)
    c: DistanceX(g0) = 79
    c: DistanceY(g0) = 2
FEATURE [Part::Extrusion] Extrude011  label="tagBottomCutDone"
  Base = -> Sketch011
  Dir = (1,0,0)
  DirMode = 2
  FaceMakerClass = Part::FaceMakerBullseye
  LengthFwd = 3
  LengthRev = 0
  Placement = pos=(35.5,10,0) rot=(0,0,1;0rad)
  Solid = true
  Symmetric = false
FEATURE [Sketcher::SketchObject] Sketch012
  FullyConstrained = true
  Placement = pos=(0,0,0) rot=(0.57735,0.57735,0.57735;2.0944rad)
  sketch-geometry (4):
    g0: LineSegment StartX=8 StartY=23 StartZ=0 EndX=26 EndY=23 EndZ=0
    g1: LineSegment StartX=26 StartY=23 StartZ=0 EndX=26 EndY=20 EndZ=0
    g2: LineSegment StartX=26 StartY=20 StartZ=0 EndX=8 EndY=20 EndZ=0
    g3: LineSegment StartX=8 StartY=20 StartZ=0 EndX=8 EndY=23 EndZ=0
  constraints (12):
    c: Coincident(g0,g1)
    c: Coincident(g1,g2)
    c: Coincident(g2,g3)
    c: Coincident(g3,g0)
    c: Horizontal(g0)
    c: Horizontal(g2)
    c: Vertical(g1)
    c: Vertical(g3)
    c: DistanceX(g2) = 8
    c: DistanceX(g2,g0) = 18
    c: DistanceY(g2) = 20
    c: DistanceY(g2,g0) = 3
FEATURE [Part::Extrusion] Extrude012  label="leftInCut"
  Base = -> Sketch012
  Dir = (1,0,0)
  DirMode = 2
  FaceMakerClass = Part::FaceMakerBullseye
  LengthFwd = 2
  LengthRev = 0
  Placement = pos=(72,1,0) rot=(0,0,1;0rad)
  Solid = true
  Symmetric = false
FEATURE [Sketcher::SketchObject] Sketch013
  FullyConstrained = true
  MapMode = 4
  Placement = pos=(72,1,0) rot=(0.57735,0.57735,0.57735;2.0944rad)
  Support = -> [Extrude012]
  sketch-geometry (4):
    g0: LineSegment StartX=26 StartY=19.9 StartZ=0 EndX=12 EndY=19.9 EndZ=0
    g1: LineSegment StartX=12 StartY=19.9 StartZ=0 EndX=12 EndY=22.9 EndZ=0
    g2: LineSegment StartX=12 StartY=22.9 StartZ=0 EndX=26 EndY=22.9 EndZ=0
    g3: LineSegment StartX=26 StartY=22.9 StartZ=0 EndX=26 EndY=19.9 EndZ=0
  constraints (12):
    c: Coincident(g0,g1)
    c: Coincident(g1,g2)
    c: Coincident(g2,g3)
    c: Coincident(g3,g0)
    c: Horizontal(g0)
    c: Horizontal(g2)
    c: Vertical(g1)
    c: Vertical(g3)
    c: DistanceX(g0,g0) = 14
    c: DistanceX(g1) = 12
    c: DistanceY(g1) = 22.9
    c: DistanceY(g1,g1) = 3
FEATURE [Part::Extrusion] Extrude013  label="sdCut"
  Base = -> Sketch013
  Dir = (1,0,0)
  DirMode = 2
  FaceMakerClass = Part::FaceMakerBullseye
  LengthFwd = 2
  LengthRev = 0
  Placement = pos=(-72,0,0) rot=(0,0,1;0rad)
  Solid = true
  Symmetric = false
FEATURE [Part::MultiFuse] Fusion017  label="bottomCutsHorDone"
  Shapes = -> [Extrude013,Extrude012]
FEATURE [Sketcher::SketchObject] Sketch014
  FullyConstrained = true
  Placement = pos=(0,0,0) rot=(1,0,0;1.5708rad)
  sketch-geometry (8):
    g0: ArcOfCircle CenterX=12.75 CenterY=15.23 CenterZ=0 NormalX=0 NormalY=0 NormalZ=1 AngleXU=0 Radius=0.9 StartAngle=1.5708 EndAngle=3.14159
    g1: ArcOfCircle CenterX=16.35 CenterY=15.23 CenterZ=0 NormalX=0 NormalY=0 NormalZ=1 AngleXU=0 Radius=0.9 StartAngle=8e-16 EndAngle=1.5708
    g2: ArcOfCircle CenterX=16.35 CenterY=14.43 CenterZ=0 NormalX=0 NormalY=0 NormalZ=1 AngleXU=0 Radius=0.9 StartAngle=4.71239 EndAngle=6.28319
    g3: ArcOfCircle CenterX=12.75 CenterY=14.43 CenterZ=0 NormalX=0 NormalY=0 NormalZ=1 AngleXU=0 Radius=0.9 StartAngle=3.14159 EndAngle=4.71239
    g4: LineSegment StartX=12.75 StartY=16.13 StartZ=0 EndX=16.35 EndY=16.13 EndZ=0
    g5: LineSegment StartX=17.25 StartY=15.23 StartZ=0 EndX=17.25 EndY=14.43 EndZ=0
    g6: LineSegment StartX=16.35 StartY=13.53 StartZ=0 EndX=12.75 EndY=13.53 EndZ=0
    g7: LineSegment StartX=11.85 StartY=14.43 StartZ=0 EndX=11.85 EndY=15.23 EndZ=0
  constraints (28):
    c: Coincident(g4,g0)
    c: Coincident(g4,g1)
    c: Horizontal(g4)
    c: Coincident(g5,g1)
    c: Coincident(g5,g2)
    c: Coincident(g6,g2)
    c: Coincident(g6,g3)
    c: Horizontal(g6)
    c: Coincident(g7,g3)
    c: Coincident(g7,g0)
    c: Vertical(g7)
    c: Radius(g0) = 0.9
    c: DistanceY(g0,g0) = 0
    c: Angle(g3) = 1.5708
    c: DistanceY(g3,g3) = 0
    c: DistanceY(g3,g0) = 0.8
    c: DistanceY(g3) = 14.43
    c: Radius(g3) = 0.9
    c: Radius(g2) = 0.9
    c: Radius(g1) = 0.9
    c: DistanceX(g6,g6) = 3.6
    c: DistanceX(g3) = 12.75
    c: DistanceY(g1,g1) = 0
    c: DistanceX(g2,g2) = 0
    c: Angle(g1) = 1.5708
    c: Angle(g2) = 1.5708
    c: Vertical(g5)
    c: DistanceX(g0,g0) = 0
FEATURE [Sketcher::SketchObject] Sketch015
  FullyConstrained = true
  Placement = pos=(0,0,0) rot=(1,0,0;1.5708rad)
  sketch-geometry (8):
    g0: ArcOfCircle CenterX=11.7 CenterY=15.45 CenterZ=0 NormalX=0 NormalY=0 NormalZ=1 AngleXU=0 Radius=0.9 StartAngle=1.5708 EndAngle=3.14159
    g1: ArcOfCircle CenterX=17.4 CenterY=15.45 CenterZ=0 NormalX=0 NormalY=0 NormalZ=1 AngleXU=0 Radius=0.9 StartAngle=4e-16 EndAngle=1.5708
    g2: ArcOfCircle CenterX=16.8 CenterY=14.2 CenterZ=0 NormalX=0 NormalY=0 NormalZ=1 AngleXU=0 Radius=1.5 StartAngle=4.71239 EndAngle=6.28319
    g3: ArcOfCircle CenterX=12.3 CenterY=14.2 CenterZ=0 NormalX=0 NormalY=0 NormalZ=1 AngleXU=0 Radius=1.5 StartAngle=3.14159 EndAngle=4.71239
    g4: LineSegment StartX=11.7 StartY=16.35 StartZ=0 EndX=17.4 EndY=16.35 EndZ=0
    g5: LineSegment StartX=18.3 StartY=15.45 StartZ=0 EndX=18.3 EndY=14.2 EndZ=0
    g6: LineSegment StartX=16.8 StartY=12.7 StartZ=0 EndX=12.3 EndY=12.7 EndZ=0
    g7: LineSegment StartX=10.8 StartY=14.2 StartZ=0 EndX=10.8 EndY=15.45 EndZ=0
  constraints (28):
    c: Coincident(g4,g0)
    c: Coincident(g4,g1)
    c: Horizontal(g4)
    c: Coincident(g5,g1)
    c: Coincident(g5,g2)
    c: Coincident(g6,g2)
    c: Coincident(g6,g3)
    c: Horizontal(g6)
    c: Coincident(g7,g3)
    c: Coincident(g7,g0)
    c: Vertical(g7)
    c: Radius(g0) = 0.9
    c: DistanceY(g0,g0) = 0
    c: Angle(g3) = 1.5708
    c: DistanceY(g3,g3) = 0
    c: DistanceY(g3,g0) = 1.25
    c: DistanceY(g3) = 14.2
    c: Radius(g3) = 1.5
    c: Radius(g2) = 1.5
    c: Radius(g1) = 0.9
    c: DistanceX(g6,g6) = 4.5
    c: DistanceX(g3) = 12.3
    c: DistanceY(g1,g1) = 0
    c: DistanceX(g2,g2) = 0
    c: Angle(g1) = 1.5708
    c: Angle(g2) = 1.5708
    c: Vertical(g5)
    c: DistanceX(g0,g0) = 0
FEATURE [Part::Extrusion] Extrude014
  Base = -> Sketch014
  Dir = (0,-1,2e-16)
  DirMode = 2
  FaceMakerClass = Part::FaceMakerBullseye
  LengthFwd = 2.75
  LengthRev = 0
  Placement = pos=(0,2,0) rot=(0,0,1;0rad)
  Solid = true
  Symmetric = false
FEATURE [Part::Extrusion] Extrude015
  Base = -> Sketch015
  Dir = (0,-1,2e-16)
  DirMode = 2
  FaceMakerClass = Part::FaceMakerBullseye
  LengthFwd = 1
  LengthRev = 0
  Placement = pos=(0,2.5,0) rot=(0,0,1;0rad)
  Solid = true
  Symmetric = false
FEATURE [Part::MultiFuse] Fusion018  label="button1"
  Shapes = -> [Extrude014,Extrude015]
FEATURE [Sketcher::SketchObject] Sketch018
  FullyConstrained = true
  Placement = pos=(0,0,0) rot=(1,0,0;1.5708rad)
  sketch-geometry (8):
    g0: ArcOfCircle CenterX=11.8 CenterY=15.45 CenterZ=0 NormalX=0 NormalY=0 NormalZ=1 AngleXU=0 Radius=1.25 StartAngle=1.5708 EndAngle=3.14159
    g1: ArcOfCircle CenterX=17.3 CenterY=15.45 CenterZ=0 NormalX=0 NormalY=0 NormalZ=1 AngleXU=0 Radius=1.25 StartAngle=-9e-16 EndAngle=1.5708
    g2: ArcOfCircle CenterX=16.8 CenterY=14.2 CenterZ=0 NormalX=0 NormalY=0 NormalZ=1 AngleXU=0 Radius=1.75 StartAngle=4.71239 EndAngle=6.28319
    g3: ArcOfCircle CenterX=12.3 CenterY=14.2 CenterZ=0 NormalX=0 NormalY=0 NormalZ=1 AngleXU=0 Radius=1.75 StartAngle=3.14159 EndAngle=4.71239
    g4: LineSegment StartX=11.8 StartY=16.7 StartZ=0 EndX=17.3 EndY=16.7 EndZ=0
    g5: LineSegment StartX=18.55 StartY=15.45 StartZ=0 EndX=18.55 EndY=14.2 EndZ=0
    g6: LineSegment StartX=16.8 StartY=12.45 StartZ=0 EndX=12.3 EndY=12.45 EndZ=0
    g7: LineSegment StartX=10.55 StartY=14.2 StartZ=0 EndX=10.55 EndY=15.45 EndZ=0
  constraints (28):
    c: Coincident(g4,g0)
    c: Coincident(g4,g1)
    c: Horizontal(g4)
    c: Coincident(g5,g1)
    c: Coincident(g5,g2)
    c: Coincident(g6,g2)
    c: Coincident(g6,g3)
    c: Horizontal(g6)
    c: Coincident(g7,g3)
    c: Coincident(g7,g0)
    c: Vertical(g7)
    c: Radius(g0) = 1.25
    c: DistanceY(g0,g0) = 0
    c: Angle(g3) = 1.5708
    c: DistanceY(g3,g3) = 0
    c: DistanceY(g3,g0) = 1.25
    c: DistanceY(g3) = 14.2
    c: Radius(g3) = 1.75
    c: Radius(g2) = 1.75
    c: Radius(g1) = 1.25
    c: DistanceX(g6,g6) = 4.5
    c: DistanceX(g3) = 12.3
    c: DistanceY(g1,g1) = 0
    c: DistanceX(g2,g2) = 0
    c: Angle(g1) = 1.5708
    c: Angle(g2) = 1.5708
    c: Vertical(g5)
    c: DistanceX(g0,g0) = 0
FEATURE [Part::Extrusion] Extrude018  label="buttonCuts"
  Base = -> Sketch018
  Dir = (0,-1,2e-16)
  DirMode = 2
  FaceMakerClass = Part::FaceMakerBullseye
  LengthFwd = 0.6
  LengthRev = 0
  Placement = pos=(0,2,0) rot=(0,0,1;0rad)
  Solid = true
  Symmetric = false
FEATURE [Sketcher::SketchObject] Sketch019
  FullyConstrained = true
  Placement = pos=(0,0,0) rot=(1,0,0;1.5708rad)
  sketch-geometry (8):
    g0: ArcOfCircle CenterX=11.8 CenterY=15.45 CenterZ=0 NormalX=0 NormalY=0 NormalZ=1 AngleXU=0 Radius=1.25 StartAngle=1.5708 EndAngle=3.14159
    g1: ArcOfCircle CenterX=17.3 CenterY=15.45 CenterZ=0 NormalX=0 NormalY=0 NormalZ=1 AngleXU=0 Radius=1.25 StartAngle=-9e-16 EndAngle=1.5708
    g2: ArcOfCircle CenterX=16.8 CenterY=14.2 CenterZ=0 NormalX=0 NormalY=0 NormalZ=1 AngleXU=0 Radius=1.75 StartAngle=4.71239 EndAngle=6.28319
    g3: ArcOfCircle CenterX=12.3 CenterY=14.2 CenterZ=0 NormalX=0 NormalY=0 NormalZ=1 AngleXU=0 Radius=1.75 StartAngle=3.14159 EndAngle=4.71239
    g4: LineSegment StartX=11.8 StartY=16.7 StartZ=0 EndX=17.3 EndY=16.7 EndZ=0
    g5: LineSegment StartX=18.55 StartY=15.45 StartZ=0 EndX=18.55 EndY=14.2 EndZ=0
    g6: LineSegment StartX=16.8 StartY=12.45 StartZ=0 EndX=12.3 EndY=12.45 EndZ=0
    g7: LineSegment StartX=10.55 StartY=14.2 StartZ=0 EndX=10.55 EndY=15.45 EndZ=0
  constraints (28):
    c: Coincident(g4,g0)
    c: Coincident(g4,g1)
    c: Horizontal(g4)
    c: Coincident(g5,g1)
    c: Coincident(g5,g2)
    c: Coincident(g6,g2)
    c: Coincident(g6,g3)
    c: Horizontal(g6)
    c: Coincident(g7,g3)
    c: Coincident(g7,g0)
    c: Vertical(g7)
    c: Radius(g0) = 1.25
    c: DistanceY(g0,g0) = 0
    c: Angle(g3) = 1.5708
    c: DistanceY(g3,g3) = 0
    c: DistanceY(g3,g0) = 1.25
    c: DistanceY(g3) = 14.2
    c: Radius(g3) = 1.75
    c: Radius(g2) = 1.75
    c: Radius(g1) = 1.25
    c: DistanceX(g6,g6) = 4.5
    c: DistanceX(g3) = 12.3
    c: DistanceY(g1,g1) = 0
    c: DistanceX(g2,g2) = 0
    c: Angle(g1) = 1.5708
    c: Angle(g2) = 1.5708
    c: Vertical(g5)
    c: DistanceX(g0,g0) = 0
FEATURE [Part::Extrusion] Extrude019  label="buttonCuts001"
  Base = -> Sketch019
  Dir = (0,-1,2e-16)
  DirMode = 2
  FaceMakerClass = Part::FaceMakerBullseye
  LengthFwd = 0.6
  LengthRev = 0
  Placement = pos=(32.5,2,0) rot=(0,0,1;0rad)
  Solid = true
  Symmetric = false
FEATURE [Part::MultiFuse] Fusion022  label="bottomButtonCuts002"
  Shapes = -> [Extrude019,Extrude018]
FEATURE [Mesh::Feature] wearableV5_LoGo  label="wearableV5-LoGo"
  Placement = pos=(-17.25,10,1) rot=(0,0,1;0rad)
FEATURE [Sketcher::SketchObject] Sketch020
  FullyConstrained = true
  sketch-geometry (15):
    g0: LineSegment StartX=3 StartY=56.25 StartZ=0 EndX=3 EndY=82 EndZ=0
    g1: LineSegment StartX=3 StartY=82 StartZ=0 EndX=13 EndY=82 EndZ=0
    g2: LineSegment StartX=13 StartY=82 StartZ=0 EndX=13 EndY=78.75 EndZ=0
    g3: LineSegment StartX=13 StartY=78.75 StartZ=0 EndX=71 EndY=78.75 EndZ=0
    g4: LineSegment StartX=71 StartY=78.75 StartZ=0 EndX=71 EndY=60 EndZ=0
    g5: Circle CenterX=5.45 CenterY=77.95 CenterZ=0 NormalX=0 NormalY=0 NormalZ=1 AngleXU=0 Radius=1.65
    g6: Circle CenterX=63.15 CenterY=62.65 CenterZ=0 NormalX=0 NormalY=0 NormalZ=1 AngleXU=0 Radius=1.65
    g7: Circle CenterX=63.15 CenterY=75.4 CenterZ=0 NormalX=0 NormalY=0 NormalZ=1 AngleXU=0 Radius=1.65
    g8: LineSegment StartX=11.75 StartY=34.86 StartZ=0 EndX=61 EndY=34.86 EndZ=0
    g9: LineSegment StartX=61 StartY=34.86 StartZ=0 EndX=61 EndY=60 EndZ=0
    g10: LineSegment StartX=61 StartY=60 StartZ=0 EndX=71 EndY=60 EndZ=0
    g11: ArcOfCircle CenterX=6.5 CenterY=41 CenterZ=0 NormalX=0 NormalY=0 NormalZ=1 AngleXU=0 Radius=5.25 StartAngle=1e-16 EndAngle=1.26095
    g12: LineSegment StartX=11.75 StartY=34.86 StartZ=0 EndX=11.75 EndY=41 EndZ=0
    g13: ArcOfCircle CenterX=6.5 CenterY=51 CenterZ=0 NormalX=0 NormalY=0 NormalZ=1 AngleXU=0 Radius=5.25 StartAngle=5.02223 EndAngle=7.85398
    g14: LineSegment StartX=3 StartY=56.25 StartZ=0 EndX=6.5 EndY=56.25 EndZ=0
  constraints (47):
    c: DistanceX(g0) = 3
    c: Vertical(g0)
    c: Coincident(g0,g1)
    c: Coincident(g2,g1)
    c: Vertical(g2)
    c: Coincident(g3,g2)
    c: Horizontal(g3)
    c: Coincident(g4,g3)
    c: Horizontal(g1)
    c: Vertical(g4)
    c: DistanceY(g0) = 82
    c: DistanceX(g0,g1) = 10
    c: DistanceY(g2,g1) = 3.25
    c: DistanceX(g3) = 71
    c: Horizontal(g8)
    c: Coincident(g9,g8)
    c: Vertical(g9)
    c: Coincident(g10,g9)
    c: Coincident(g10,g4)
    c: Horizontal(g10)
    c: DistanceY(g9) = 60
    c: DistanceX(g5) = 5.45
    c: DistanceY(g5) = 77.95
    c: Equal(g5,g7)
    c: Equal(g5,g6)
    c: Radius(g5) = 1.65
    c: DistanceX(g6,g7) = 0
    c: DistanceY(g6,g7) = 12.75
    c: DistanceX(g8) = 61
    c: DistanceY(g8) = 34.86
    c: DistanceX(g6) = 63.15
    c: DistanceY(g6) = 62.65
    c: Coincident(g12,g8)
    c: Coincident(g12,g11)
    c: Vertical(g12)
    c: DistanceX(g11) = 6.5
    c: DistanceY(g11) = 41
    c: DistanceY(g11,g11) = 0
    c: Radius(g11) = 5.25
    c: Coincident(g11,g13)
    c: Radius(g13) = 5.25
    c: DistanceX(g11,g13) = 0
    c: DistanceY(g11,g13) = 10
    c: Coincident(g14,g0)
    c: Coincident(g14,g13)
    c: Horizontal(g14)
    c: DistanceX(g13,g13) = 0
FEATURE [Part::Feature] Part__Feature063  label="5862K223_Neodymium Magnet"
  Placement = pos=(6.5,41,24) rot=(1,0,0;1.5708rad)
  shape: bbox 6.873 x 6.873 x 3.175 mm, 14 faces (baked)
FEATURE [Part::Feature] Part__Feature064  label="92125A051_18-8 Stainless Steel Hex Drive Flat Head Screw"
  Placement = pos=(6.5,41,19) rot=(0,0,-1;1.5708rad)
  shape: bbox 4.001 x 4.001 x 5.163 mm, 46 faces (baked)
FEATURE [Part::Extrusion] Extrude020  label="sensorHold002"
  Base = -> Sketch020
  Dir = (0,0,1)
  DirMode = 2
  FaceMakerClass = Part::FaceMakerBullseye
  LengthFwd = 4
  LengthRev = 0
  Placement = pos=(0,0,13) rot=(0,0,1;0rad)
  Solid = true
  Symmetric = false
FEATURE [Sketcher::SketchObject] Sketch021
  FullyConstrained = true
  Placement = pos=(0,0,0) rot=(1,0,0;1.5708rad)
  sketch-geometry (10):
    g0: LineSegment StartX=65 StartY=28.5 StartZ=0 EndX=71 EndY=28.5 EndZ=0
    g1: LineSegment StartX=71 StartY=28.5 StartZ=0 EndX=71 EndY=2.5 EndZ=0
    g2: LineSegment StartX=71 StartY=2.5 StartZ=0 EndX=65 EndY=2.5 EndZ=0
    g3: LineSegment StartX=65 StartY=2.5 StartZ=0 EndX=65 EndY=9 EndZ=0
    g4: LineSegment StartX=65 StartY=9 StartZ=0 EndX=67 EndY=9 EndZ=0
    g5: LineSegment StartX=67 StartY=9 StartZ=0 EndX=67 EndY=22 EndZ=0
    g6: LineSegment StartX=67 StartY=22 StartZ=0 EndX=65 EndY=22 EndZ=0
    g7: LineSegment StartX=65 StartY=22 StartZ=0 EndX=65 EndY=28.5 EndZ=0
    g8: Circle CenterX=67.85 CenterY=25.7 CenterZ=0 NormalX=0 NormalY=0 NormalZ=1 AngleXU=0 Radius=1.65
    g9: Circle CenterX=67.85 CenterY=5.4 CenterZ=0 NormalX=0 NormalY=0 NormalZ=1 AngleXU=0 Radius=1.65
  constraints (30):
    c: Horizontal(g0)
    c: Coincident(g1,g0)
    c: Vertical(g1)
    c: Coincident(g2,g1)
    c: Horizontal(g2)
    c: Coincident(g3,g2)
    c: Vertical(g3)
    c: Horizontal(g4)
    c: Coincident(g6,g5)
    c: Horizontal(g6)
    c: Coincident(g7,g0)
    c: Vertical(g7)
    c: Vertical(g5)
    c: DistanceX(g1) = 71
    c: DistanceY(g1) = 2.5
    c: DistanceX(g2,g1) = 6
    c: Coincident(g3,g4)
    c: DistanceY(g3,g3) = 6.5
    c: Coincident(g4,g5)
    c: DistanceX(g4,g4) = 2
    c: DistanceX(g3,g6) = 0
    c: Coincident(g6,g7)
    c: DistanceY(g7,g7) = 6.5
    c: DistanceY(g5,g5) = 13
    c: DistanceX(g8,g9) = 0
    c: DistanceX(g9) = 67.85
    c: DistanceY(g9) = 5.4
    c: DistanceY(g9,g8) = 20.3
    c: Equal(g8,g9)
    c: Radius(g8) = 1.65
FEATURE [Part::Extrusion] Extrude021  label="gpsHold"
  Base = -> Sketch021
  Dir = (0,-1,-3e-16)
  DirMode = 2
  FaceMakerClass = Part::FaceMakerBullseye
  LengthFwd = 5
  LengthRev = 0
  Placement = pos=(0,78.75,0) rot=(0,0,1;0rad)
  Solid = true
  Symmetric = false
FEATURE [Part::Box] Box005  label="sensorHoldIPSCut"
  AttacherType = Attacher::AttachEngine3D
  Height = 10
  Length = 48
  Placement = pos=(13,34,15.25) rot=(0,0,1;0rad)
  Width = 45
FEATURE [Part::Cut] Cut007  label="SensorHold"
  Base = -> Extrude020
  Tool = -> Box005
FEATURE [Sketcher::SketchObject] Sketch022
  FullyConstrained = true
  sketch-geometry (3):
    g0: Circle CenterX=37.45 CenterY=61.7 CenterZ=0 NormalX=0 NormalY=0 NormalZ=1 AngleXU=0 Radius=0.75
    g1: Circle CenterX=42.85 CenterY=62.65 CenterZ=0 NormalX=0 NormalY=0 NormalZ=1 AngleXU=0 Radius=1
    g2: Circle CenterX=42.85 CenterY=75.35 CenterZ=0 NormalX=0 NormalY=0 NormalZ=1 AngleXU=0 Radius=1
  constraints (9):
    c: Radius(g0) = 0.75
    c: Equal(g1,g2)
    c: Radius(g1) = 1
    c: DistanceX(g2,g1) = 0
    c: DistanceY(g1,g2) = 12.7
    c: DistanceX(g1) = 42.85
    c: DistanceY(g1) = 62.65
    c: DistanceY(g0) = 61.7
    c: DistanceX(g0) = 37.45
FEATURE [Part::Extrusion] Extrude022
  Base = -> Sketch022
  Dir = (0,0,1)
  DirMode = 2
  FaceMakerClass = Part::FaceMakerBullseye
  LengthFwd = 8
  LengthRev = 0
  Placement = pos=(0,0,6) rot=(0,0,1;0rad)
  Solid = true
  Symmetric = false
FEATURE [Part::Feature] Part__Feature065  label="5862K223_Neodymium Magnet001"
  Placement = pos=(6.5,41,20) rot=(1,0,0;1.5708rad)
  shape: bbox 6.873 x 6.873 x 3.175 mm, 14 faces (baked)
FEATURE [Sketcher::SketchObject] Sketch024
  FullyConstrained = true
  sketch-geometry (5):
    g0: ArcOfCircle CenterX=6.5 CenterY=41 CenterZ=0 NormalX=0 NormalY=0 NormalZ=1 AngleXU=0 Radius=5 StartAngle=4.71239 EndAngle=7.85398
    g1: LineSegment StartX=6.5 StartY=46 StartZ=0 EndX=2 EndY=46 EndZ=0
    g2: LineSegment StartX=6.5 StartY=36 StartZ=0 EndX=2 EndY=36 EndZ=0
    g3: LineSegment StartX=2 StartY=46 StartZ=0 EndX=2 EndY=36 EndZ=0
    g4: Circle CenterX=6.5 CenterY=41 CenterZ=0 NormalX=0 NormalY=0 NormalZ=1 AngleXU=0 Radius=1.65
  constraints (15):
    c: Coincident(g1,g0)
    c: Coincident(g2,g0)
    c: Horizontal(g2)
    c: Coincident(g3,g1)
    c: Coincident(g3,g2)
    c: Vertical(g3)
    c: Horizontal(g1)
    c: DistanceX(g0,g0) = 0
    c: DistanceX(g2) = 2
    c: DistanceY(g2) = 36
    c: DistanceY(g2,g1) = 10
    c: Angle(g0) = 3.14159
    c: DistanceX(g0) = 6.5
    c: Coincident(g4,g0)
    c: Radius(g4) = 1.65
FEATURE [Part::Extrusion] Extrude023  label="magnetHold"
  Base = -> Sketch024
  Dir = (0,0,1)
  DirMode = 2
  FaceMakerClass = Part::FaceMakerBullseye
  LengthFwd = 5
  LengthRev = 0
  Placement = pos=(0,0,13.25) rot=(0,0,1;0rad)
  Solid = true
  Symmetric = false
FEATURE [Sketcher::SketchObject] Sketch027
  FullyConstrained = true
  sketch-geometry (5):
    g0: ArcOfCircle CenterX=6.5 CenterY=41 CenterZ=0 NormalX=0 NormalY=0 NormalZ=1 AngleXU=0 Radius=5 StartAngle=4.71239 EndAngle=7.85398
    g1: LineSegment StartX=6.5 StartY=46 StartZ=0 EndX=2 EndY=46 EndZ=0
    g2: LineSegment StartX=6.5 StartY=36 StartZ=0 EndX=2 EndY=36 EndZ=0
    g3: LineSegment StartX=2 StartY=46 StartZ=0 EndX=2 EndY=36 EndZ=0
    g4: Circle CenterX=6.5 CenterY=41 CenterZ=0 NormalX=0 NormalY=0 NormalZ=1 AngleXU=0 Radius=1.65
  constraints (15):
    c: Coincident(g1,g0)
    c: Coincident(g2,g0)
    c: Horizontal(g2)
    c: Coincident(g3,g1)
    c: Coincident(g3,g2)
    c: Vertical(g3)
    c: Horizontal(g1)
    c: DistanceX(g0,g0) = 0
    c: DistanceX(g2) = 2
    c: DistanceY(g2) = 36
    c: DistanceY(g2,g1) = 10
    c: Angle(g0) = 3.14159
    c: DistanceX(g0) = 6.5
    c: Coincident(g4,g0)
    c: Radius(g4) = 1.65
FEATURE [Part::Extrusion] Extrude024  label="sensorMountHold001"
  Base = -> Sketch027
  Dir = (0,0,1)
  DirMode = 2
  FaceMakerClass = Part::FaceMakerBullseye
  LengthFwd = 5
  LengthRev = 0
  Placement = pos=(0,10,13.25) rot=(0,0,1;0rad)
  Solid = true
  Symmetric = false
FEATURE [Sketcher::SketchObject] Sketch028
  FullyConstrained = true
  sketch-geometry (6):
    g0: LineSegment StartX=8.25 StartY=46.0503 StartZ=0 EndX=13 EndY=46.0503 EndZ=0
    g1: LineSegment StartX=13 StartY=46.0503 StartZ=0 EndX=13 EndY=59 EndZ=0
    g2: LineSegment StartX=13 StartY=59 StartZ=0 EndX=3 EndY=59 EndZ=0
    g3: LineSegment StartX=3 StartY=59 StartZ=0 EndX=3 EndY=56.25 EndZ=0
    g4: LineSegment StartX=3 StartY=56.25 StartZ=0 EndX=6.5 EndY=56.25 EndZ=0
    g5: ArcOfCircle CenterX=6.5 CenterY=51 CenterZ=0 NormalX=0 NormalY=0 NormalZ=1 AngleXU=0 Radius=5.25 StartAngle=5.05223 EndAngle=7.85398
  constraints (19):
    c: Horizontal(g0)
    c: Coincident(g1,g0)
    c: Vertical(g1)
    c: Coincident(g2,g1)
    c: Horizontal(g2)
    c: Coincident(g3,g2)
    c: Vertical(g3)
    c: Coincident(g4,g3)
    c: Coincident(g5,g4)
    c: Coincident(g5,g0)
    c: Radius(g5) = 5.25
    c: DistanceX(g5) = 6.5
    c: DistanceY(g5) = 51
    c: Horizontal(g4)
    c: DistanceX(g0) = 8.25
    c: DistanceX(g5,g4) = 0
    c: DistanceX(g0) = 13
    c: DistanceX(g3) = 3
    c: DistanceY(g3,g2) = 2.75
FEATURE [Part::Extrusion] Extrude025
  Base = -> Sketch028
  Dir = (0,0,1)
  DirMode = 2
  FaceMakerClass = Part::FaceMakerBullseye
  LengthFwd = 1.5
  LengthRev = 0
  Placement = pos=(0,0,17) rot=(0,0,1;0rad)
  Solid = true
  Symmetric = false
FEATURE [Part::Box] Box006  label="Cube"
  AttacherType = Attacher::AttachEngine3D
  Height = 4
  Length = 10
  Placement = pos=(3,46.05,18.5) rot=(0,0,1;0rad)
  Width = 12.95
FEATURE [Part::MultiFuse] Fusion025  label="sennsorHold"
  Shapes = -> [Box006,Extrude025,Extrude022,Cut007,Fillet003,Extrude021]
FEATURE [Part::Cylinder] Cylinder022
  Angle = 360
  AttacherType = Attacher::AttachEngine3D
  FirstAngle = 0
  Height = 10
  Placement = pos=(6.5,51,13.03) rot=(0,0,1;0rad)
  Radius = 1.15
  SecondAngle = 0
FEATURE [Part::Cut] Cut008  label="sensorHold003"
  Base = -> Fusion025
  Tool = -> Cylinder022
FEATURE [Part::Feature] Part__Feature066  label="91290A125_Alloy Steel Socket Head Screw"
  Placement = pos=(42,85.5,14) rot=(1,0,0;3.14159rad)
  shape: bbox 5.501 x 5.501 x 28.29 mm, 108 faces (baked)
FEATURE [Part::Cylinder] Cylinder023  label="m3Cut"
  Angle = 360
  AttacherType = Attacher::AttachEngine3D
  FirstAngle = 0
  Height = 10
  Placement = pos=(42,85.5,0) rot=(0,0,1;0rad)
  Radius = 1.75
  SecondAngle = 0
FEATURE [Part::Cylinder] Cylinder024  label="m3HeadCut001"
  Angle = 360
  AttacherType = Attacher::AttachEngine3D
  FirstAngle = 0
  Height = 4
  Placement = pos=(42,85.5,0) rot=(0,0,1;0rad)
  Radius = 3
  SecondAngle = 0
FEATURE [Part::MultiFuse] Fusion026  label="m3Cut001"
  Shapes = -> [Cylinder024,Cylinder023]
FEATURE [Part::Cylinder] Cylinder025  label="m3keep"
  Angle = 360
  AttacherType = Attacher::AttachEngine3D
  FirstAngle = 0
  Height = 5
  Placement = pos=(42,85.5,2) rot=(0,0,1;0rad)
  Radius = 5
  SecondAngle = 0
FEATURE [Part::MultiFuse] Fusion027  label="bottom004"
  Shapes = -> [Cut,Cylinder025]
FEATURE [Part::MultiFuse] Fusion028  label="bottom005"
  Shapes = -> [Extrude023,Extrude024,Fusion027,Extrude009]
FEATURE [Part::MultiFuse] Fusion029
  Shapes = -> [Fusion026,Extrude011]
FEATURE [Part::Cut] Cut009  label="bottom006"
  Base = -> Fusion028
  Tool = -> Fusion029
FEATURE [Part::Cut] Cut010  label="bottom007"
  Base = -> Cut009
  Tool = -> Extrude007
FEATURE [Part::Box] Box008  label="bottom009"
  AttacherType = Attacher::AttachEngine3D
  Height = 39
  Length = 70
  Placement = pos=(2,2,2) rot=(0,0,1;0rad)
  Width = 87
FEATURE [Part::Fillet] Fillet007  label="topCUt"
  Base = -> Box008
  Edges = 12 edges: [Edge1 r=2,Edge2 r=1,Edge3 r=2,Edge4 r=2,Edge5 r=2,Edge6 r=1,Edge7 r=2,Edge8 r=2,Edge9 r=2,Edge10 r=1,Edge11 r=2,Edge12 r=1]
  Placement = pos=(0,0,-9) rot=(0,0,1;0rad)
FEATURE [Part::Cut] Cut011  label="top002"
  Base = -> Fillet005
  Placement = pos=(0,0,-2) rot=(0,0,1;0rad)
  Tool = -> Fillet007
FEATURE [Sketcher::SketchObject] Sketch029
  FullyConstrained = true
  sketch-geometry (23):
    g0: ArcOfCircle CenterX=42 CenterY=85.5 CenterZ=0 NormalX=0 NormalY=0 NormalZ=1 AngleXU=0 Radius=5 StartAngle=2.43401 EndAngle=6.99077
    g1: ArcOfCircle CenterX=4 CenterY=87 CenterZ=0 NormalX=0 NormalY=0 NormalZ=1 AngleXU=0 Radius=1.75 StartAngle=1.5708 EndAngle=3.14159
    g2: LineSegment StartX=4 StartY=88.75 StartZ=0 EndX=6 EndY=88.75 EndZ=0
    g3: LineSegment StartX=6 StartY=85 StartZ=0 EndX=2.25 EndY=85 EndZ=0
    g4: LineSegment StartX=2.25 StartY=87 StartZ=0 EndX=2.25 EndY=85 EndZ=0
    g5: LineSegment StartX=70 StartY=88.75 StartZ=0 EndX=68 EndY=88.75 EndZ=0
    g6: LineSegment StartX=68 StartY=88.75 StartZ=0 EndX=68 EndY=85 EndZ=0
    g7: LineSegment StartX=68 StartY=85 StartZ=0 EndX=71.75 EndY=85 EndZ=0
    g8: LineSegment StartX=71.75 StartY=85 StartZ=0 EndX=71.75 EndY=87 EndZ=0
    g9: ArcOfCircle CenterX=70 CenterY=87 CenterZ=0 NormalX=0 NormalY=0 NormalZ=1 AngleXU=0 Radius=1.75 StartAngle=2.8e-15 EndAngle=1.5708
    g10: ArcOfCircle CenterX=70 CenterY=4 CenterZ=0 NormalX=0 NormalY=0 NormalZ=1 AngleXU=0 Radius=1.75 StartAngle=4.71239 EndAngle=6.28319
    g11: LineSegment StartX=70 StartY=2.25 StartZ=0 EndX=68 EndY=2.25 EndZ=0
    g12: LineSegment StartX=68 StartY=2.25 StartZ=0 EndX=68 EndY=6 EndZ=0
    g13: LineSegment StartX=68 StartY=6 StartZ=0 EndX=71.75 EndY=6 EndZ=0
    g14: LineSegment StartX=71.75 StartY=6 StartZ=0 EndX=71.75 EndY=4 EndZ=0
    g15: LineSegment StartX=2.25 StartY=6 StartZ=0 EndX=6 EndY=6 EndZ=0
    g16: LineSegment StartX=6 StartY=6 StartZ=0 EndX=6 EndY=2.25 EndZ=0
    g17: LineSegment StartX=6 StartY=2.25 StartZ=0 EndX=4 EndY=2.25 EndZ=0
    g18: LineSegment StartX=2.25 StartY=6 StartZ=0 EndX=2.25 EndY=4 EndZ=0
    g19: ArcOfCircle CenterX=4 CenterY=4 CenterZ=0 NormalX=0 NormalY=0 NormalZ=1 AngleXU=0 Radius=1.75 StartAngle=3.14159 EndAngle=4.71239
    g20: LineSegment StartX=6 StartY=88.75 StartZ=0 EndX=6 EndY=85 EndZ=0
    g21: LineSegment StartX=38.2003 StartY=88.75 StartZ=0 EndX=45.7997 EndY=88.75 EndZ=0
    g22: Circle CenterX=42 CenterY=85.5 CenterZ=0 NormalX=0 NormalY=0 NormalZ=1 AngleXU=0 Radius=2
  constraints (73):
    c: DistanceX(g0) = 42
    c: DistanceY(g0) = 85.5
    c: Radius(g0) = 5
    c: Coincident(g2,g1)
    c: Horizontal(g2)
    c: Horizontal(g3)
    c: Coincident(g4,g1)
    c: Coincident(g4,g3)
    c: Coincident(g6,g5)
    c: Vertical(g6)
    c: Coincident(g7,g6)
    c: Horizontal(g7)
    c: Coincident(g9,g5)
    c: Coincident(g9,g8)
    c: Coincident(g11,g10)
    c: Coincident(g12,g11)
    c: Coincident(g13,g12)
    c: Coincident(g14,g13)
    c: Coincident(g14,g10)
    c: Vertical(g14)
    c: Coincident(g16,g15)
    c: Vertical(g16)
    c: Coincident(g17,g16)
    c: Horizontal(g17)
    c: Coincident(g18,g15)
    c: Coincident(g19,g17)
    c: Coincident(g19,g18)
    c: Radius(g1) = 1.75
    c: DistanceX(g1) = 4
    c: DistanceY(g1) = 87
    c: Vertical(g4)
    c: DistanceY(g3,g1) = 2
    c: DistanceX(g1,g2) = 2
    c: DistanceY(g1,g1) = 0
    c: Angle(g1) = 1.5708
    c: DistanceY(g6,g3) = 0
    c: Radius(g9) = 1.75
    c: Horizontal(g5)
    c: Vertical(g8)
    c: DistanceY(g8,g1) = 0
    c: DistanceX(g6) = 68
    c: Coincident(g7,g8)
    c: DistanceY(g8,g9) = 0
    c: DistanceX(g9,g5) = 0
    c: Coincident(g20,g2)
    c: Coincident(g20,g3)
    c: Vertical(g20)
    c: DistanceX(g6,g9) = 2
    c: DistanceX(g19,g1) = 0
    c: Vertical(g18)
    c: Angle(g19) = 1.5708
    c: DistanceX(g17,g16) = 2
    c: DistanceX(g17,g19) = 0
    c: DistanceX(g15,g3) = 0
    c: Horizontal(g15)
    c: DistanceY(g18,g15) = 2
    c: DistanceY(g19) = 4
    c: DistanceY(g19,g10) = 0
    c: DistanceX(g9,g10) = 0
    c: Vertical(g12)
    c: Horizontal(g13)
    c: Horizontal(g11)
    c: DistanceX(g10,g10) = 0
    c: DistanceX(g12,g10) = 2
    c: DistanceY(g10,g12) = 2
    c: DistanceY(g11,g16) = 0
    c: DistanceX(g13,g7) = 0
    c: DistanceY(g5,g0) = 0
    c: Coincident(g21,g0)
    c: Coincident(g0,g21)
    c: Horizontal(g21)
    c: Coincident(g22,g0)
    c: Radius(g22) = 2
FEATURE [Part::Extrusion] Extrude026  label="topHoldCornerIn"
  Base = -> Sketch029
  Dir = (0,0,1)
  DirMode = 2
  FaceMakerClass = Part::FaceMakerBullseye
  LengthFwd = 6
  LengthRev = 0
  Placement = pos=(0,0,24.25) rot=(0,0,1;0rad)
  Solid = true
  Symmetric = false
FEATURE [Sketcher::SketchObject] Sketch030
  FullyConstrained = true
  sketch-geometry (5):
    g0: ArcOfCircle CenterX=6.5 CenterY=41 CenterZ=0 NormalX=0 NormalY=0 NormalZ=1 AngleXU=0 Radius=4.75 StartAngle=4.71239 EndAngle=7.85398
    g1: LineSegment StartX=6.5 StartY=36.25 StartZ=0 EndX=2.25 EndY=36.25 EndZ=0
    g2: LineSegment StartX=2.25 StartY=36.25 StartZ=0 EndX=2.25 EndY=45.75 EndZ=0
    g3: LineSegment StartX=2.25 StartY=45.75 StartZ=0 EndX=6.5 EndY=45.75 EndZ=0
    g4: Circle CenterX=6.5 CenterY=41 CenterZ=0 NormalX=0 NormalY=0 NormalZ=1 AngleXU=0 Radius=1.65
  constraints (15):
    c: Coincident(g1,g0)
    c: Horizontal(g1)
    c: Coincident(g2,g1)
    c: Vertical(g2)
    c: Coincident(g3,g2)
    c: Coincident(g3,g0)
    c: Horizontal(g3)
    c: DistanceX(g0) = 6.5
    c: Radius(g0) = 4.75
    c: Angle(g0) = 3.14159
    c: DistanceX(g0,g0) = 0
    c: DistanceX(g2,g0) = 4.25
    c: DistanceY(g0) = 41
    c: Coincident(g4,g0)
    c: Radius(g4) = 1.65
FEATURE [Part::Extrusion] Extrude027  label="topMagnetHoldIn"
  Base = -> Sketch030
  Dir = (0,0,1)
  DirMode = 2
  FaceMakerClass = Part::FaceMakerBullseye
  LengthFwd = 4.5
  LengthRev = 0
  Placement = pos=(0,0,25.75) rot=(0,0,1;0rad)
  Solid = true
  Symmetric = false
FEATURE [Part::MultiFuse] Fusion  label="bottomIn"
  Shapes = -> [Fillet004,Cut010]
FEATURE [Part::MultiFuse] Fusion030  label="bottomCuts"
  Shapes = -> [Fusion017,Fusion022,Extrude004]
FEATURE [Part::Cut] Cut012  label="bottom010"
  Base = -> Fusion
  Tool = -> Fusion030
FEATURE [Part::MultiFuse] Fusion031  label="top003"
  Shapes = -> [Extrude027,Extrude026,Cut011]
FEATURE [Part::Cut] Cut013  label="top004"
  Base = -> Fusion031
  Tool = -> Part__Feature060
FEATURE [Part::Fillet] Fillet008  label="bottom011"
  Base = -> Cut012
  Edges = 38 edges r=0.5: [Edge23,Edge118,Edge120,Edge141,Edge187,Edge189,Edge191,Edge193,Edge195,Edge197,Edge212,Edge214,Edge216,Edge218,Edge220,Edge222,Edge250,Edge252,Edge254,Edge256,Edge275,Edge277,Edge279,Edge281,Edge283,Edge285,Edge287,Edge288,Edge291,Edge293,Edge295,Edge297,Edge299,Edge300,Edge327,Edge328,Edge329,+1 more]
FEATURE [Part::Box] Box009  label="top005"
  AttacherType = Attacher::AttachEngine3D
  Height = 5
  Length = 74
  Placement = pos=(0,0,27) rot=(0,0,1;0rad)
  Width = 91
FEATURE [Part::Box] Box010  label="bottom012"
  AttacherType = Attacher::AttachEngine3D
  Height = 39
  Length = 70
  Placement = pos=(2,2,2) rot=(0,0,1;0rad)
  Width = 87
FEATURE [Part::Fillet] Fillet009  label="top008"
  Base = -> Box009
  Edges = 8 edges r=1.95: [Edge1,Edge2,Edge3,Edge5,Edge6,Edge7,Edge10,Edge12]
  Placement = pos=(0,0,2) rot=(0,0,1;0rad)
FEATURE [Part::Fillet] Fillet010  label="topCUt001"
  Base = -> Box010
  Edges = 12 edges: [Edge1 r=2,Edge2 r=1,Edge3 r=2,Edge4 r=2,Edge5 r=2,Edge6 r=1,Edge7 r=2,Edge8 r=2,Edge9 r=2,Edge10 r=1,Edge11 r=2,Edge12 r=1]
  Placement = pos=(0,0,-9) rot=(0,0,1;0rad)
FEATURE [Part::Cut] Cut014  label="top006"
  Base = -> Fillet009
  Placement = pos=(0,0,-2) rot=(0,0,1;0rad)
  Tool = -> Fillet010
FEATURE [Part::Feature] Part__Feature067  label="logoTopCut001"
  Placement = pos=(27,-2,35) rot=(-1,0,0;1.5708rad)
  shape: bbox 22.79 x 17.08 x 8 mm, 886 faces (baked)
FEATURE [Sketcher::SketchObject] Sketch031
  FullyConstrained = true
  sketch-geometry (23):
    g0: ArcOfCircle CenterX=42 CenterY=85.5 CenterZ=0 NormalX=0 NormalY=0 NormalZ=1 AngleXU=0 Radius=5 StartAngle=2.43401 EndAngle=6.99077
    g1: ArcOfCircle CenterX=4 CenterY=87 CenterZ=0 NormalX=0 NormalY=0 NormalZ=1 AngleXU=0 Radius=1.75 StartAngle=1.5708 EndAngle=3.14159
    g2: LineSegment StartX=4 StartY=88.75 StartZ=0 EndX=6 EndY=88.75 EndZ=0
    g3: LineSegment StartX=6 StartY=85 StartZ=0 EndX=2.25 EndY=85 EndZ=0
    g4: LineSegment StartX=2.25 StartY=87 StartZ=0 EndX=2.25 EndY=85 EndZ=0
    g5: LineSegment StartX=70 StartY=88.75 StartZ=0 EndX=68 EndY=88.75 EndZ=0
    g6: LineSegment StartX=68 StartY=88.75 StartZ=0 EndX=68 EndY=85 EndZ=0
    g7: LineSegment StartX=68 StartY=85 StartZ=0 EndX=71.75 EndY=85 EndZ=0
    g8: LineSegment StartX=71.75 StartY=85 StartZ=0 EndX=71.75 EndY=87 EndZ=0
    g9: ArcOfCircle CenterX=70 CenterY=87 CenterZ=0 NormalX=0 NormalY=0 NormalZ=1 AngleXU=0 Radius=1.75 StartAngle=2.8e-15 EndAngle=1.5708
    g10: ArcOfCircle CenterX=70 CenterY=4 CenterZ=0 NormalX=0 NormalY=0 NormalZ=1 AngleXU=0 Radius=1.75 StartAngle=4.71239 EndAngle=6.28319
    g11: LineSegment StartX=70 StartY=2.25 StartZ=0 EndX=68 EndY=2.25 EndZ=0
    g12: LineSegment StartX=68 StartY=2.25 StartZ=0 EndX=68 EndY=6 EndZ=0
    g13: LineSegment StartX=68 StartY=6 StartZ=0 EndX=71.75 EndY=6 EndZ=0
    g14: LineSegment StartX=71.75 StartY=6 StartZ=0 EndX=71.75 EndY=4 EndZ=0
    g15: LineSegment StartX=2.25 StartY=6 StartZ=0 EndX=6 EndY=6 EndZ=0
    g16: LineSegment StartX=6 StartY=6 StartZ=0 EndX=6 EndY=2.25 EndZ=0
    g17: LineSegment StartX=6 StartY=2.25 StartZ=0 EndX=4 EndY=2.25 EndZ=0
    g18: LineSegment StartX=2.25 StartY=6 StartZ=0 EndX=2.25 EndY=4 EndZ=0
    g19: ArcOfCircle CenterX=4 CenterY=4 CenterZ=0 NormalX=0 NormalY=0 NormalZ=1 AngleXU=0 Radius=1.75 StartAngle=3.14159 EndAngle=4.71239
    g20: LineSegment StartX=6 StartY=88.75 StartZ=0 EndX=6 EndY=85 EndZ=0
    g21: LineSegment StartX=38.2003 StartY=88.75 StartZ=0 EndX=45.7997 EndY=88.75 EndZ=0
    g22: Circle CenterX=42 CenterY=85.5 CenterZ=0 NormalX=0 NormalY=0 NormalZ=1 AngleXU=0 Radius=2
  constraints (73):
    c: DistanceX(g0) = 42
    c: DistanceY(g0) = 85.5
    c: Radius(g0) = 5
    c: Coincident(g2,g1)
    c: Horizontal(g2)
    c: Horizontal(g3)
    c: Coincident(g4,g1)
    c: Coincident(g4,g3)
    c: Coincident(g6,g5)
    c: Vertical(g6)
    c: Coincident(g7,g6)
    c: Horizontal(g7)
    c: Coincident(g9,g5)
    c: Coincident(g9,g8)
    c: Coincident(g11,g10)
    c: Coincident(g12,g11)
    c: Coincident(g13,g12)
    c: Coincident(g14,g13)
    c: Coincident(g14,g10)
    c: Vertical(g14)
    c: Coincident(g16,g15)
    c: Vertical(g16)
    c: Coincident(g17,g16)
    c: Horizontal(g17)
    c: Coincident(g18,g15)
    c: Coincident(g19,g17)
    c: Coincident(g19,g18)
    c: Radius(g1) = 1.75
    c: DistanceX(g1) = 4
    c: DistanceY(g1) = 87
    c: Vertical(g4)
    c: DistanceY(g3,g1) = 2
    c: DistanceX(g1,g2) = 2
    c: DistanceY(g1,g1) = 0
    c: Angle(g1) = 1.5708
    c: DistanceY(g6,g3) = 0
    c: Radius(g9) = 1.75
    c: Horizontal(g5)
    c: Vertical(g8)
    c: DistanceY(g8,g1) = 0
    c: DistanceX(g6) = 68
    c: Coincident(g7,g8)
    c: DistanceY(g8,g9) = 0
    c: DistanceX(g9,g5) = 0
    c: Coincident(g20,g2)
    c: Coincident(g20,g3)
    c: Vertical(g20)
    c: DistanceX(g6,g9) = 2
    c: DistanceX(g19,g1) = 0
    c: Vertical(g18)
    c: Angle(g19) = 1.5708
    c: DistanceX(g17,g16) = 2
    c: DistanceX(g17,g19) = 0
    c: DistanceX(g15,g3) = 0
    c: Horizontal(g15)
    c: DistanceY(g18,g15) = 2
    c: DistanceY(g19) = 4
    c: DistanceY(g19,g10) = 0
    c: DistanceX(g9,g10) = 0
    c: Vertical(g12)
    c: Horizontal(g13)
    c: Horizontal(g11)
    c: DistanceX(g10,g10) = 0
    c: DistanceX(g12,g10) = 2
    c: DistanceY(g10,g12) = 2
    c: DistanceY(g11,g16) = 0
    c: DistanceX(g13,g7) = 0
    c: DistanceY(g5,g0) = 0
    c: Coincident(g21,g0)
    c: Coincident(g0,g21)
    c: Horizontal(g21)
    c: Coincident(g22,g0)
    c: Radius(g22) = 2
FEATURE [Part::Extrusion] Extrude028  label="topHoldCornerIn001"
  Base = -> Sketch031
  Dir = (0,0,1)
  DirMode = 2
  FaceMakerClass = Part::FaceMakerBullseye
  LengthFwd = 6
  LengthRev = 0
  Placement = pos=(0,0,24.25) rot=(0,0,1;0rad)
  Solid = true
  Symmetric = false
FEATURE [Sketcher::SketchObject] Sketch032
  FullyConstrained = true
  sketch-geometry (5):
    g0: ArcOfCircle CenterX=6.5 CenterY=41 CenterZ=0 NormalX=0 NormalY=0 NormalZ=1 AngleXU=0 Radius=4.75 StartAngle=4.71239 EndAngle=7.85398
    g1: LineSegment StartX=6.5 StartY=36.25 StartZ=0 EndX=2.25 EndY=36.25 EndZ=0
    g2: LineSegment StartX=2.25 StartY=36.25 StartZ=0 EndX=2.25 EndY=45.75 EndZ=0
    g3: LineSegment StartX=2.25 StartY=45.75 StartZ=0 EndX=6.5 EndY=45.75 EndZ=0
    g4: Circle CenterX=6.5 CenterY=41 CenterZ=0 NormalX=0 NormalY=0 NormalZ=1 AngleXU=0 Radius=1.65
  constraints (15):
    c: Coincident(g1,g0)
    c: Horizontal(g1)
    c: Coincident(g2,g1)
    c: Vertical(g2)
    c: Coincident(g3,g2)
    c: Coincident(g3,g0)
    c: Horizontal(g3)
    c: DistanceX(g0) = 6.5
    c: Radius(g0) = 4.75
    c: Angle(g0) = 3.14159
    c: DistanceX(g0,g0) = 0
    c: DistanceX(g2,g0) = 4.25
    c: DistanceY(g0) = 41
    c: Coincident(g4,g0)
    c: Radius(g4) = 1.65
FEATURE [Part::Extrusion] Extrude029  label="topMagnetHoldIn001"
  Base = -> Sketch032
  Dir = (0,0,1)
  DirMode = 2
  FaceMakerClass = Part::FaceMakerBullseye
  LengthFwd = 4.5
  LengthRev = 0
  Placement = pos=(0,0,25.75) rot=(0,0,1;0rad)
  Solid = true
  Symmetric = false
FEATURE [Part::MultiFuse] Fusion032  label="top009"
  Shapes = -> [Extrude029,Extrude028,Cut014]
FEATURE [Part::Cut] Cut015  label="top007"
  Base = -> Fusion032
  Tool = -> Part__Feature067
